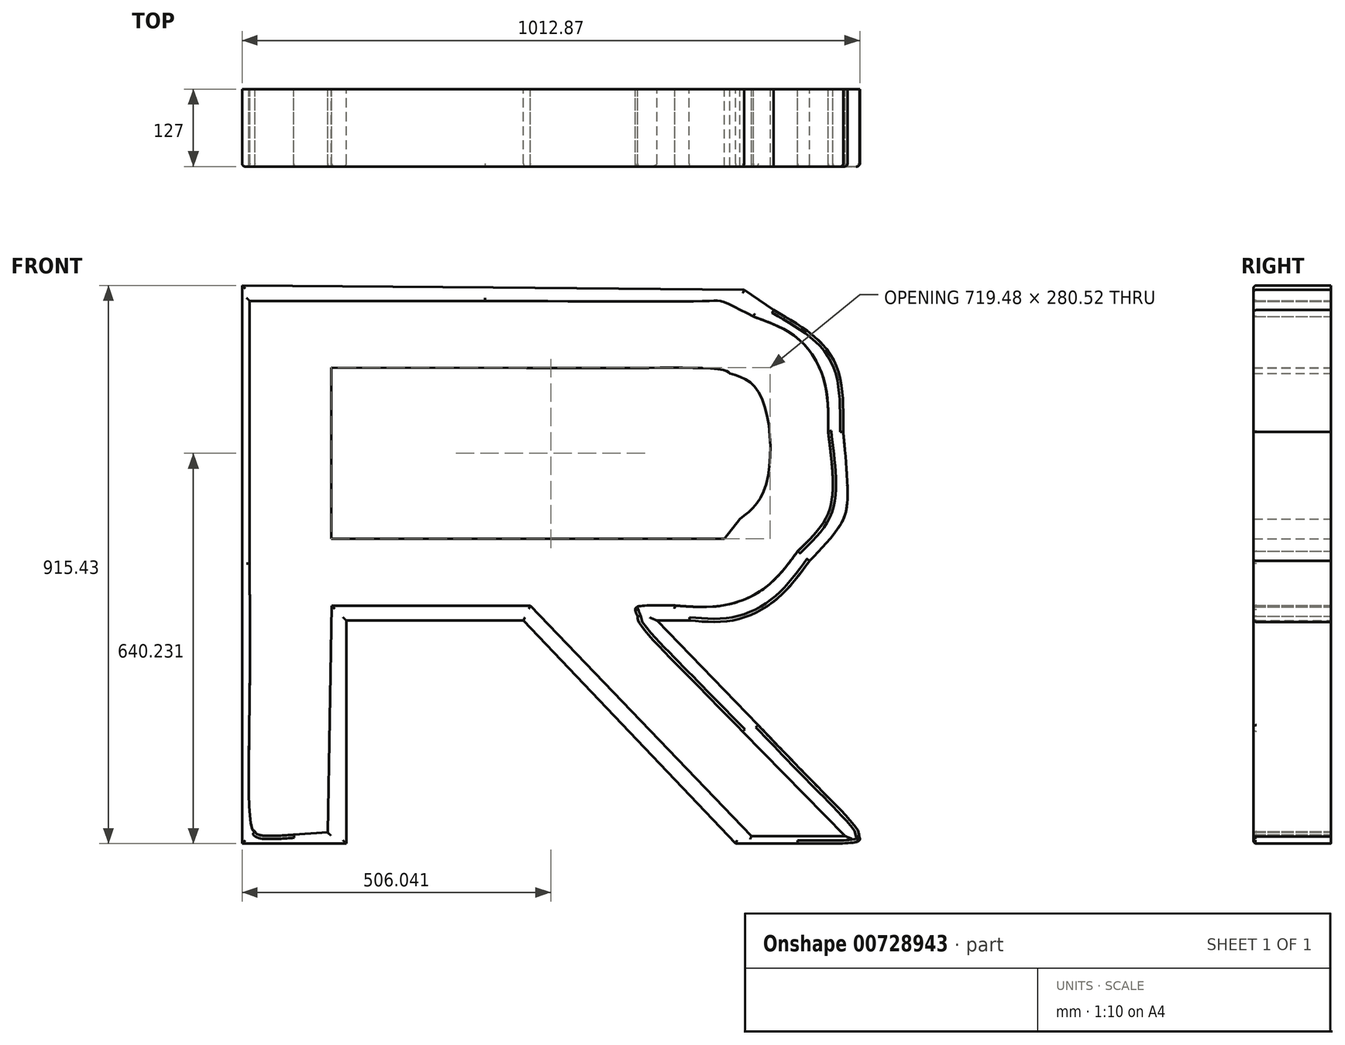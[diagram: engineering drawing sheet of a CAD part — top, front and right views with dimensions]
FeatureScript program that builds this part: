
annotation { "Feature Type Name" : "Feature", "Feature Type Description" : "" }
export const myFeature = defineFeature(function(context is Context, id is Id, definition is map)
    precondition{}
    {
        {
            var Q0;
            Q0=qCreatedBy(makeId("Front.planeOp"),FACE);
            var sketch = newSketch(context, id + "F0", { "sketchPlane" : qUnion([Q0])});
            skFitSpline(sketch, "E0", {"points": [v(-4513.08, -1878.1) * mm, v(-4548.72, -1872.9) * mm, v(-4580.06, -1866.5) * mm, v(-4582.7, -1863.84) * mm]});
            skFitSpline(sketch, "E1", {"points": [v(-4582.7, -1863.84) * mm, v(-4587.16, -1859.4) * mm, v(-4686.02, -165.4) * mm, v(-4686.02, -93.63) * mm]});
            skFitSpline(sketch, "E2", {"points": [v(-4686.02, -93.63) * mm, v(-4686.02, -76.02) * mm, v(-4679.1, -61.78) * mm, v(-4670.55, -61.78) * mm]});
            skFitSpline(sketch, "E3", {"points": [v(-4670.55, -61.78) * mm, v(-4662.04, -61.78) * mm, v(-4570.6, -244.2) * mm, v(-4467.36, -467.16) * mm]});
            skFitSpline(sketch, "E4", {"points": [v(-4467.36, -467.16) * mm, v(-4364.12, -690.12) * mm, v(-4179.05, -1088.06) * mm, v(-4056.11, -1351.47) * mm]});
            skFitSpline(sketch, "E5", {"points": [v(-4056.11, -1351.47) * mm, v(-3933.17, -1614.87) * mm, v(-3832.58, -1840.38) * mm, v(-3832.58, -1852.6) * mm]});
            skFitSpline(sketch, "E6", {"points": [v(-3832.58, -1852.6) * mm, v(-3832.58, -1871.46) * mm, v(-3846.64, -1876) * mm, v(-3925.86, -1882.7) * mm]});
            skFitSpline(sketch, "E7", {"points": [v(-3925.86, -1882.7) * mm, v(-4048.62, -1893.07) * mm, v(-4430.8, -1890.08) * mm, v(-4513.08, -1878.1) * mm]});
            skFitSpline(sketch, "E8", {"points": [v(-3879.02, -1844.36) * mm, v(-3866.96, -1832.3) * mm, v(-3906.6, -1744.18) * mm, v(-4421.11, -639.04) * mm]});
            skFitSpline(sketch, "E9", {"points": [v(-4421.11, -639.04) * mm, v(-4595.2, -265.1) * mm, v(-4644.19, -169.51) * mm, v(-4647.22, -197.77) * mm]});
            skFitSpline(sketch, "E10", {"points": [v(-4647.22, -197.77) * mm, v(-4650.89, -231.93) * mm, v(-4564.93, -1832.53) * mm, v(-4559.1, -1838.57) * mm]});
            skFitSpline(sketch, "E11", {"points": [v(-4559.1, -1838.57) * mm, v(-4534.28, -1864.33) * mm, v(-3904.35, -1869.69) * mm, v(-3879.02, -1844.36) * mm]});
            skFitSpline(sketch, "E12", {"points": [v(-5033.5, -1799.55) * mm, v(-5198.5, -1753.5) * mm, v(-5300.18, -1716.7) * mm, v(-5421.74, -1659.07) * mm]});
            skFitSpline(sketch, "E13", {"points": [v(-5421.74, -1659.07) * mm, v(-5492.65, -1625.45) * mm, v(-5504.3, -1615.6) * mm, v(-5499.25, -1593.5) * mm]});
            skFitSpline(sketch, "E14", {"points": [v(-5499.25, -1593.5) * mm, v(-5494.86, -1574.27) * mm, v(-5054.5, -397.2) * mm, v(-4942.58, -105.51) * mm]});
            skFitSpline(sketch, "E15", {"points": [v(-4942.58, -105.51) * mm, v(-4906.1, -10.43) * mm, v(-4900.2, -88.58) * mm, v(-4878.5, -955.17) * mm]});
            skFitSpline(sketch, "E16", {"points": [v(-4878.5, -955.17) * mm, v(-4866.7, -1426.06) * mm, v(-4859.55, -1818.19) * mm, v(-4862.6, -1826.57) * mm]});
            skFitSpline(sketch, "E17", {"points": [v(-4862.6, -1826.57) * mm, v(-4869.7, -1846.13) * mm, v(-4862.58, -1847.26) * mm, v(-5033.5, -1799.55) * mm]});
            skFitSpline(sketch, "E18", {"points": [v(-4886.44, -1747.32) * mm, v(-4889.85, -1715.47) * mm, v(-4898.96, -1379.43) * mm, v(-4906.7, -1000.56) * mm]});
            skFitSpline(sketch, "E19", {"points": [v(-4906.7, -1000.56) * mm, v(-4914.43, -621.7) * mm, v(-4924.18, -280.69) * mm, v(-4928.36, -242.77) * mm]});
            skFitSpline(sketch, "E20", {"points": [v(-5195.5, -864.56) * mm, v(-5338.25, -1244.47) * mm, v(-5458.03, -1566.94) * mm, v(-5461.69, -1581.16) * mm]});
            skFitSpline(sketch, "E21", {"points": [v(-5461.69, -1581.16) * mm, v(-5467.6, -1604.15) * mm, v(-5453.6, -1613.24) * mm, v(-5335.45, -1663.1) * mm]});
            skFitSpline(sketch, "E22", {"points": [v(-5335.45, -1663.1) * mm, v(-5217.3, -1712.99) * mm, v(-4937.34, -1803.14) * mm, v(-4895.91, -1804.66) * mm]});
            skFitSpline(sketch, "E23", {"points": [v(-4895.91, -1804.66) * mm, v(-4884.45, -1805.08) * mm, v(-4881.9, -1789.73) * mm, v(-4886.44, -1747.32) * mm]});
            skLineSegment(sketch, "E24", {"start": v(-4928.36, -242.77) * mm, "end": v(-4935.96, -173.83) * mm});
            skLineSegment(sketch, "E25", {"start": v(-4935.96, -173.83) * mm, "end": v(-5195.5, -864.56) * mm});
            skFitSpline(sketch, "E26", {"points": [v(-5758.92, -1450.29) * mm, v(-5985.16, -1262.43) * mm, v(-6141.2, -1100.12) * mm, v(-6134.22, -1059.86) * mm]});
            skFitSpline(sketch, "E27", {"points": [v(-6134.22, -1059.86) * mm, v(-6131.22, -1042.48) * mm, v(-5234.38, -58.31) * mm, v(-5181.72, -14.6) * mm]});
            skFitSpline(sketch, "E28", {"points": [v(-5181.72, -14.6) * mm, v(-5164.94, -0.68) * mm, v(-5160.85, -0.7) * mm, v(-5155.78, -14.68) * mm]});
            skFitSpline(sketch, "E29", {"points": [v(-5155.78, -14.68) * mm, v(-5146.02, -41.6) * mm, v(-5688.86, -1469.2) * mm, v(-5710.15, -1472.64) * mm]});
            skFitSpline(sketch, "E30", {"points": [v(-5710.15, -1472.64) * mm, v(-5720.2, -1474.27) * mm, v(-5742.15, -1464.2) * mm, v(-5758.92, -1450.29) * mm]});
            skFitSpline(sketch, "E31", {"points": [v(-5583.89, -1110.3) * mm, v(-5340.19, -464.36) * mm, v(-5189.83, -61.78) * mm, v(-5192.28, -61.78) * mm]});
            skFitSpline(sketch, "E32", {"points": [v(-5192.28, -61.78) * mm, v(-5193.68, -61.78) * mm, v(-5375.19, -257.92) * mm, v(-5595.63, -497.64) * mm]});
            skFitSpline(sketch, "E33", {"points": [v(-5595.63, -497.64) * mm, v(-5816.08, -737.37) * mm, v(-6023.27, -962.22) * mm, v(-6056.06, -997.33) * mm]});
            skFitSpline(sketch, "E34", {"points": [v(-6080.96, -1107.05) * mm, v(-5997.1, -1217.95) * mm, v(-5722.2, -1461.2) * mm, v(-5709.04, -1436.14) * mm]});
            skFitSpline(sketch, "E35", {"points": [v(-5709.04, -1436.14) * mm, v(-5704.72, -1427.92) * mm, v(-5648.4, -1281.28) * mm, v(-5583.89, -1110.3) * mm]});
            skLineSegment(sketch, "E36", {"start": v(-6056.06, -997.33) * mm, "end": v(-6115.67, -1061.15) * mm});
            skLineSegment(sketch, "E37", {"start": v(-6115.67, -1061.15) * mm, "end": v(-6080.96, -1107.05) * mm});
            skFitSpline(sketch, "E38", {"points": [v(-6376.64, -717.1) * mm, v(-6465.1, -554.38) * mm, v(-6517.72, -425.18) * mm, v(-6512.5, -383.52) * mm]});
            skFitSpline(sketch, "E39", {"points": [v(-6512.5, -383.52) * mm, v(-6509.12, -356.55) * mm, v(-6448.9, -325.3) * mm, v(-5938.45, -85.66) * mm]});
            skFitSpline(sketch, "E40", {"points": [v(-5938.45, -85.66) * mm, v(-5624.8, 61.59) * mm, v(-5362.42, 182.06) * mm, v(-5355.38, 182.06) * mm]});
            skFitSpline(sketch, "E41", {"points": [v(-5355.38, 182.06) * mm, v(-5348.35, 182.06) * mm, v(-5344.37, 174.42) * mm, v(-5346.54, 165.09) * mm]});
            skFitSpline(sketch, "E42", {"points": [v(-5346.54, 165.09) * mm, v(-5353.35, 135.75) * mm, v(-6262.79, -854.26) * mm, v(-6282.92, -854.26) * mm]});
            skFitSpline(sketch, "E43", {"points": [v(-6282.92, -854.26) * mm, v(-6294.77, -854.26) * mm, v(-6330.5, -801.99) * mm, v(-6376.64, -717.1) * mm]});
            skFitSpline(sketch, "E44", {"points": [v(-5831.8, -342.2) * mm, v(-5615.18, -104.15) * mm, v(-5427.1, 102.77) * mm, v(-5413.85, 117.6) * mm]});
            skFitSpline(sketch, "E45", {"points": [v(-5413.85, 117.6) * mm, v(-5398.94, 134.3) * mm, v(-5598.63, 46.37) * mm, v(-5937.04, -112.76) * mm]});
            skFitSpline(sketch, "E46", {"points": [v(-5937.04, -112.76) * mm, v(-6238.06, -254.3) * mm, v(-6486.6, -372.02) * mm, v(-6489.34, -374.36) * mm]});
            skFitSpline(sketch, "E47", {"points": [v(-6489.34, -374.36) * mm, v(-6506.31, -388.79) * mm, v(-6417.14, -598.64) * mm, v(-6332.34, -743.85) * mm]});
            skFitSpline(sketch, "E48", {"points": [v(-6253.05, -803.85) * mm, v(-6237.97, -787.99) * mm, v(-6048.41, -580.24) * mm, v(-5831.8, -342.2) * mm]});
            skLineSegment(sketch, "E49", {"start": v(-6332.34, -743.85) * mm, "end": v(-6280.45, -832.7) * mm});
            skLineSegment(sketch, "E50", {"start": v(-6280.45, -832.7) * mm, "end": v(-6253.05, -803.85) * mm});
            skFitSpline(sketch, "E51", {"points": [v(3214.4, -607.33) * mm, v(3181.1, -589.95) * mm, v(3147.6, -532.2) * mm, v(3159.56, -512.83) * mm]});
            skFitSpline(sketch, "E52", {"points": [v(3159.56, -512.83) * mm, v(3171.55, -493.43) * mm, v(3228.61, -498.8) * mm, v(3244.73, -520.84) * mm]});
            skFitSpline(sketch, "E53", {"points": [v(3244.73, -520.84) * mm, v(3253.05, -532.22) * mm, v(3265.83, -537.06) * mm, v(3274.1, -531.95) * mm]});
            skFitSpline(sketch, "E54", {"points": [v(3274.1, -531.95) * mm, v(3292.4, -520.64) * mm, v(3269.27, -488.5) * mm, v(3242.83, -488.5) * mm]});
            skFitSpline(sketch, "E55", {"points": [v(3242.83, -488.5) * mm, v(3212.18, -488.5) * mm, v(3165.63, -430.83) * mm, v(3165.63, -392.87) * mm]});
            skFitSpline(sketch, "E56", {"points": [v(3165.63, -392.87) * mm, v(3165.63, -335.43) * mm, v(3202.8, -300.08) * mm, v(3263.16, -300.08) * mm]});
            skFitSpline(sketch, "E57", {"points": [v(3263.16, -300.08) * mm, v(3302.3, -300.08) * mm, v(3320.03, -306.86) * mm, v(3337.62, -328.58) * mm]});
            skFitSpline(sketch, "E58", {"points": [v(3337.62, -328.58) * mm, v(3375.45, -375.3) * mm, v(3368.13, -403.15) * mm, v(3318.03, -403.15) * mm]});
            skFitSpline(sketch, "E59", {"points": [v(3318.03, -403.15) * mm, v(3294.56, -403.15) * mm, v(3275.36, -397.67) * mm, v(3275.36, -390.96) * mm]});
            skFitSpline(sketch, "E60", {"points": [v(3275.36, -390.96) * mm, v(3275.36, -384.26) * mm, v(3269.87, -378.77) * mm, v(3263.16, -378.77) * mm]});
            skFitSpline(sketch, "E61", {"points": [v(3263.16, -378.77) * mm, v(3234.41, -378.77) * mm, v(3254.73, -400.93) * mm, v(3299.66, -418.58) * mm]});
            skFitSpline(sketch, "E62", {"points": [v(3299.66, -418.58) * mm, v(3354.1, -439.97) * mm, v(3378.57, -483.66) * mm, v(3366.6, -538.12) * mm]});
            skFitSpline(sketch, "E63", {"points": [v(3366.6, -538.12) * mm, v(3352.4, -602.85) * mm, v(3274.05, -638.47) * mm, v(3214.4, -607.33) * mm]});
            skFitSpline(sketch, "E64", {"points": [v(3317.82, -566.22) * mm, v(3329.82, -554.21) * mm, v(3336.17, -531.45) * mm, v(3333.93, -508.46) * mm]});
            skFitSpline(sketch, "E65", {"points": [v(3333.93, -508.46) * mm, v(3330.95, -478) * mm, v(3319.87, -464.82) * mm, v(3277.73, -441.64) * mm]});
            skFitSpline(sketch, "E66", {"points": [v(3277.73, -441.64) * mm, v(3237.65, -419.6) * mm, v(3226.11, -406.58) * mm, v(3228.96, -386.63) * mm]});
            skFitSpline(sketch, "E67", {"points": [v(3228.96, -386.63) * mm, v(3233.27, -356.35) * mm, v(3285.18, -343.03) * mm, v(3300.75, -368.2) * mm]});
            skFitSpline(sketch, "E68", {"points": [v(3300.75, -368.2) * mm, v(3306.17, -376.98) * mm, v(3314.43, -380.34) * mm, v(3319.1, -375.66) * mm]});
            skFitSpline(sketch, "E69", {"points": [v(3319.1, -375.66) * mm, v(3323.78, -371) * mm, v(3320.43, -358.53) * mm, v(3311.66, -347.96) * mm]});
            skFitSpline(sketch, "E70", {"points": [v(3311.66, -347.96) * mm, v(3287.48, -318.83) * mm, v(3224.3, -329.53) * mm, v(3206.32, -365.8) * mm]});
            skFitSpline(sketch, "E71", {"points": [v(3206.32, -365.8) * mm, v(3186.57, -405.64) * mm, v(3202.8, -433.32) * mm, v(3264.32, -464.7) * mm]});
            skFitSpline(sketch, "E72", {"points": [v(3264.32, -464.7) * mm, v(3305.7, -485.82) * mm, v(3312.83, -494.93) * mm, v(3309.63, -522.66) * mm]});
            skFitSpline(sketch, "E73", {"points": [v(3309.63, -522.66) * mm, v(3306.49, -549.91) * mm, v(3299.03, -556.21) * mm, v(3266.13, -559.38) * mm]});
            skFitSpline(sketch, "E74", {"points": [v(3266.13, -559.38) * mm, v(3238.78, -562.02) * mm, v(3224.14, -557.27) * mm, v(3219.1, -544.14) * mm]});
            skFitSpline(sketch, "E75", {"points": [v(3219.1, -544.14) * mm, v(3211.2, -523.53) * mm, v(3190.01, -517.9) * mm, v(3190.01, -536.4) * mm]});
            skFitSpline(sketch, "E76", {"points": [v(3190.01, -536.4) * mm, v(3190.01, -580.85) * mm, v(3281.77, -602.26) * mm, v(3317.82, -566.22) * mm]});
            skFitSpline(sketch, "E77", {"points": [v(5507.24, -600.33) * mm, v(5430.62, -559.24) * mm, v(5401.78, -465.95) * mm, v(5440.49, -384.37) * mm]});
            skFitSpline(sketch, "E78", {"points": [v(5440.49, -384.37) * mm, v(5486.58, -287.24) * mm, v(5615.75, -267.6) * mm, v(5698.52, -345.13) * mm]});
            skFitSpline(sketch, "E79", {"points": [v(5698.52, -345.13) * mm, v(5740.21, -384.19) * mm, v(5734.76, -415.43) * mm, v(5686.32, -414.96) * mm]});
            skFitSpline(sketch, "E80", {"points": [v(5686.32, -414.96) * mm, v(5664.53, -414.75) * mm, v(5636.05, -406.52) * mm, v(5623.03, -396.67) * mm]});
            skFitSpline(sketch, "E81", {"points": [v(5623.03, -396.67) * mm, v(5610.02, -386.83) * mm, v(5589.44, -378.77) * mm, v(5577.31, -378.77) * mm]});
            skFitSpline(sketch, "E82", {"points": [v(5577.31, -378.77) * mm, v(5546.4, -378.77) * mm, v(5506.5, -422.12) * mm, v(5506.5, -455.72) * mm]});
            skFitSpline(sketch, "E83", {"points": [v(5506.5, -455.72) * mm, v(5506.5, -517.6) * mm, v(5592.51, -562.23) * mm, v(5628.41, -518.98) * mm]});
            skFitSpline(sketch, "E84", {"points": [v(5628.41, -518.98) * mm, v(5648.4, -494.89) * mm, v(5712.42, -495.2) * mm, v(5721.71, -519.43) * mm]});
            skFitSpline(sketch, "E85", {"points": [v(5721.71, -519.43) * mm, v(5736.2, -557.18) * mm, v(5644.3, -622.6) * mm, v(5576.8, -622.6) * mm]});
            skFitSpline(sketch, "E86", {"points": [v(5576.8, -622.6) * mm, v(5561.4, -622.6) * mm, v(5530.1, -612.58) * mm, v(5507.24, -600.33) * mm]});
            skFitSpline(sketch, "E87", {"points": [v(5646.13, -571.89) * mm, v(5663.2, -564.1) * mm, v(5677.18, -552.54) * mm, v(5677.18, -546.2) * mm]});
            skFitSpline(sketch, "E88", {"points": [v(5677.18, -546.2) * mm, v(5677.18, -539.76) * mm, v(5667.74, -538.8) * mm, v(5655.84, -544.03) * mm]});
            skFitSpline(sketch, "E89", {"points": [v(5655.84, -544.03) * mm, v(5560.75, -585.8) * mm, v(5482.1, -547.64) * mm, v(5482.1, -459.73) * mm]});
            skFitSpline(sketch, "E90", {"points": [v(5482.1, -459.73) * mm, v(5482.1, -394.34) * mm, v(5519.02, -354.39) * mm, v(5579.44, -354.39) * mm]});
            skFitSpline(sketch, "E91", {"points": [v(5579.44, -354.39) * mm, v(5603.81, -354.39) * mm, v(5634.4, -362.44) * mm, v(5647.42, -372.29) * mm]});
            skFitSpline(sketch, "E92", {"points": [v(5647.42, -372.29) * mm, v(5677.34, -394.92) * mm, v(5690.42, -395.69) * mm, v(5682.22, -374.33) * mm]});
            skFitSpline(sketch, "E93", {"points": [v(5682.22, -374.33) * mm, v(5673.25, -350.95) * mm, v(5622.4, -330) * mm, v(5574.62, -330) * mm]});
            skFitSpline(sketch, "E94", {"points": [v(5574.62, -330) * mm, v(5461.37, -330) * mm, v(5412.53, -481.37) * mm, v(5500.86, -558.6) * mm]});
            skFitSpline(sketch, "E95", {"points": [v(5500.86, -558.6) * mm, v(5535.7, -589.07) * mm, v(5596.26, -594.6) * mm, v(5646.13, -571.89) * mm]});
            skFitSpline(sketch, "E96", {"points": [v(6475.76, -608.53) * mm, v(6440.32, -589.15) * mm, v(6420.9, -560.93) * mm, v(6420.9, -528.84) * mm]});
            skFitSpline(sketch, "E97", {"points": [v(6420.9, -528.84) * mm, v(6420.9, -505.63) * mm, v(6427.37, -500.7) * mm, v(6457.85, -500.7) * mm]});
            skFitSpline(sketch, "E98", {"points": [v(6457.85, -500.7) * mm, v(6479.46, -500.7) * mm, v(6497.73, -508.29) * mm, v(6501.83, -518.98) * mm]});
            skFitSpline(sketch, "E99", {"points": [v(6501.83, -518.98) * mm, v(6510.56, -541.73) * mm, v(6542.81, -543.18) * mm, v(6542.81, -520.83) * mm]});
            skFitSpline(sketch, "E100", {"points": [v(6542.81, -520.83) * mm, v(6542.81, -511.79) * mm, v(6520.9, -495.78) * mm, v(6494.13, -485.27) * mm]});
            skFitSpline(sketch, "E101", {"points": [v(6494.13, -485.27) * mm, v(6414.12, -453.84) * mm, v(6400.9, -369.27) * mm, v(6467.8, -316.66) * mm]});
            skFitSpline(sketch, "E102", {"points": [v(6467.8, -316.66) * mm, v(6521.92, -274.08) * mm, v(6615.96, -310.83) * mm, v(6615.96, -374.56) * mm]});
            skFitSpline(sketch, "E103", {"points": [v(6615.96, -374.56) * mm, v(6615.96, -397.75) * mm, v(6609.51, -403.15) * mm, v(6581.83, -403.15) * mm]});
            skFitSpline(sketch, "E104", {"points": [v(6581.83, -403.15) * mm, v(6563.05, -403.15) * mm, v(6541.1, -396.57) * mm, v(6533.06, -388.52) * mm]});
            skFitSpline(sketch, "E105", {"points": [v(6533.06, -388.52) * mm, v(6523.5, -378.97) * mm, v(6518.43, -378.46) * mm, v(6518.43, -387.05) * mm]});
            skFitSpline(sketch, "E106", {"points": [v(6518.43, -387.05) * mm, v(6518.43, -394.28) * mm, v(6535.1, -407.1) * mm, v(6555.49, -415.55) * mm]});
            skFitSpline(sketch, "E107", {"points": [v(6555.49, -415.55) * mm, v(6634.58, -448.3) * mm, v(6651.74, -527.75) * mm, v(6592.52, -586.97) * mm]});
            skFitSpline(sketch, "E108", {"points": [v(6592.52, -586.97) * mm, v(6555.36, -624.13) * mm, v(6517.17, -631.19) * mm, v(6475.76, -608.53) * mm]});
            skFitSpline(sketch, "E109", {"points": [v(6589, -546.64) * mm, v(6610.12, -502.37) * mm, v(6593.07, -471.59) * mm, v(6529.45, -439.13) * mm]});
            skFitSpline(sketch, "E110", {"points": [v(6529.45, -439.13) * mm, v(6491.43, -419.74) * mm, v(6481.19, -408.01) * mm, v(6484.14, -387.28) * mm]});
            skFitSpline(sketch, "E111", {"points": [v(6484.14, -387.28) * mm, v(6488.42, -357.15) * mm, v(6540.07, -342.42) * mm, v(6555.26, -367) * mm]});
            skFitSpline(sketch, "E112", {"points": [v(6555.26, -367) * mm, v(6560.28, -375.1) * mm, v(6571.23, -379.46) * mm, v(6579.61, -376.66) * mm]});
            skFitSpline(sketch, "E113", {"points": [v(6579.61, -376.66) * mm, v(6605.96, -367.88) * mm, v(6556.8, -330) * mm, v(6519.05, -330) * mm]});
            skFitSpline(sketch, "E114", {"points": [v(6519.05, -330) * mm, v(6476.1, -330) * mm, v(6454.56, -355.13) * mm, v(6459.64, -399.34) * mm]});
            skFitSpline(sketch, "E115", {"points": [v(6459.64, -399.34) * mm, v(6462.6, -425.11) * mm, v(6475.62, -439.81) * mm, v(6512.33, -458.8) * mm]});
            skFitSpline(sketch, "E116", {"points": [v(6512.33, -458.8) * mm, v(6552.4, -479.54) * mm, v(6561.1, -490.41) * mm, v(6561.1, -519.8) * mm]});
            skFitSpline(sketch, "E117", {"points": [v(6561.1, -519.8) * mm, v(6561.1, -547.97) * mm, v(6555.07, -556.4) * mm, v(6532.66, -559.58) * mm]});
            skFitSpline(sketch, "E118", {"points": [v(6532.66, -559.58) * mm, v(6517.02, -561.8) * mm, v(6493.67, -554.06) * mm, v(6480.77, -542.38) * mm]});
            skFitSpline(sketch, "E119", {"points": [v(6480.77, -542.38) * mm, v(6449.35, -513.95) * mm, v(6435.36, -530.48) * mm, v(6464.03, -562.17) * mm]});
            skFitSpline(sketch, "E120", {"points": [v(6464.03, -562.17) * mm, v(6497.9, -599.59) * mm, v(6567.9, -590.9) * mm, v(6589, -546.64) * mm]});
            skFitSpline(sketch, "E121", {"points": [v(2275.61, -458.02) * mm, v(2275.61, -380.8) * mm, v(2270.77, -330) * mm, v(2263.42, -330) * mm]});
            skFitSpline(sketch, "E122", {"points": [v(2263.42, -330) * mm, v(2256.07, -330) * mm, v(2251.23, -380.8) * mm, v(2251.23, -458.02) * mm]});
            skFitSpline(sketch, "E123", {"points": [v(2251.23, -458.02) * mm, v(2251.23, -535.23) * mm, v(2256.07, -586.03) * mm, v(2263.42, -586.03) * mm]});
            skFitSpline(sketch, "E124", {"points": [v(2263.42, -586.03) * mm, v(2270.77, -586.03) * mm, v(2275.61, -535.23) * mm, v(2275.61, -458.02) * mm]});
            skLineSegment(sketch, "E125", {"start": v(2226.84, -458.02) * mm, "end": v(2226.84, -305.62) * mm});
            skLineSegment(sketch, "E126", {"start": v(2226.84, -305.62) * mm, "end": v(2263.42, -305.62) * mm});
            skLineSegment(sketch, "E127", {"start": v(2263.42, -305.62) * mm, "end": v(2300, -305.62) * mm});
            skLineSegment(sketch, "E128", {"start": v(2300, -305.62) * mm, "end": v(2300, -458.02) * mm});
            skLineSegment(sketch, "E129", {"start": v(2300, -458.02) * mm, "end": v(2300, -610.42) * mm});
            skLineSegment(sketch, "E130", {"start": v(2300, -610.42) * mm, "end": v(2263.42, -610.42) * mm});
            skLineSegment(sketch, "E131", {"start": v(2263.42, -610.42) * mm, "end": v(2226.84, -610.42) * mm});
            skLineSegment(sketch, "E132", {"start": v(2226.84, -610.42) * mm, "end": v(2226.84, -458.02) * mm});
            skFitSpline(sketch, "E133", {"points": [v(2616.99, -500.39) * mm, v(2616.99, -393.45) * mm, v(2616.11, -390.02) * mm, v(2585.66, -378.45) * mm]});
            skFitSpline(sketch, "E134", {"points": [v(2585.66, -378.45) * mm, v(2562.68, -369.7) * mm, v(2555.37, -359.24) * mm, v(2558.23, -339.13) * mm]});
            skFitSpline(sketch, "E135", {"points": [v(2558.23, -339.13) * mm, v(2561.87, -313.49) * mm, v(2568.04, -311.71) * mm, v(2653.56, -311.71) * mm]});
            skFitSpline(sketch, "E136", {"points": [v(2653.56, -311.71) * mm, v(2739.09, -311.71) * mm, v(2745.26, -313.49) * mm, v(2748.9, -339.13) * mm]});
            skFitSpline(sketch, "E137", {"points": [v(2748.9, -339.13) * mm, v(2751.76, -359.24) * mm, v(2744.45, -369.7) * mm, v(2721.47, -378.45) * mm]});
            skFitSpline(sketch, "E138", {"points": [v(2721.47, -378.45) * mm, v(2691.02, -390.02) * mm, v(2690.14, -393.45) * mm, v(2690.14, -500.39) * mm]});
            skFitSpline(sketch, "E139", {"points": [v(2665.76, -475.16) * mm, v(2665.76, -374.55) * mm, v(2668.01, -363.7) * mm, v(2690.14, -357.92) * mm]});
            skFitSpline(sketch, "E140", {"points": [v(2690.14, -357.92) * mm, v(2735.72, -346) * mm, v(2714.75, -330) * mm, v(2653.56, -330) * mm]});
            skFitSpline(sketch, "E141", {"points": [v(2653.56, -330) * mm, v(2592.37, -330) * mm, v(2571.41, -346) * mm, v(2616.99, -357.92) * mm]});
            skFitSpline(sketch, "E142", {"points": [v(2616.99, -357.92) * mm, v(2639.12, -363.7) * mm, v(2641.37, -374.55) * mm, v(2641.37, -475.16) * mm]});
            skFitSpline(sketch, "E143", {"points": [v(2641.37, -475.16) * mm, v(2641.37, -540.95) * mm, v(2646.33, -586.03) * mm, v(2653.56, -586.03) * mm]});
            skFitSpline(sketch, "E144", {"points": [v(2653.56, -586.03) * mm, v(2660.8, -586.03) * mm, v(2665.76, -540.95) * mm, v(2665.76, -475.16) * mm]});
            skLineSegment(sketch, "E145", {"start": v(2690.14, -500.39) * mm, "end": v(2690.14, -610.42) * mm});
            skLineSegment(sketch, "E146", {"start": v(2690.14, -610.42) * mm, "end": v(2653.56, -610.42) * mm});
            skLineSegment(sketch, "E147", {"start": v(2653.56, -610.42) * mm, "end": v(2616.99, -610.42) * mm});
            skLineSegment(sketch, "E148", {"start": v(2616.99, -610.42) * mm, "end": v(2616.99, -500.39) * mm});
            skFitSpline(sketch, "E149", {"points": [v(3717.32, -308.13) * mm, v(3802.52, -311.58) * mm, v(3805.7, -312.81) * mm, v(3805.7, -342.2) * mm]});
            skFitSpline(sketch, "E150", {"points": [v(3805.7, -342.2) * mm, v(3805.7, -368.61) * mm, v(3799.62, -373.18) * mm, v(3759.99, -376.46) * mm]});
            skFitSpline(sketch, "E151", {"points": [v(3759.99, -376.46) * mm, v(3702.05, -381.25) * mm, v(3697.47, -412.18) * mm, v(3753.9, -417.62) * mm]});
            skFitSpline(sketch, "E152", {"points": [v(3753.9, -417.62) * mm, v(3788.73, -420.98) * mm, v(3793.98, -426.22) * mm, v(3797.34, -461.07) * mm]});
            skFitSpline(sketch, "E153", {"points": [v(3797.34, -461.07) * mm, v(3801, -499.07) * mm, v(3799.38, -500.7) * mm, v(3757.71, -500.7) * mm]});
            skFitSpline(sketch, "E154", {"points": [v(3757.71, -500.7) * mm, v(3696.23, -500.7) * mm, v(3698.2, -534.47) * mm, v(3759.99, -539.58) * mm]});
            skFitSpline(sketch, "E155", {"points": [v(3759.99, -539.58) * mm, v(3799.62, -542.86) * mm, v(3805.7, -547.42) * mm, v(3805.7, -573.84) * mm]});
            skFitSpline(sketch, "E156", {"points": [v(3805.7, -573.84) * mm, v(3805.7, -603.22) * mm, v(3802.52, -604.45) * mm, v(3717.32, -607.9) * mm]});
            skLineSegment(sketch, "E157", {"start": v(3628.92, -458.02) * mm, "end": v(3628.92, -304.55) * mm});
            skLineSegment(sketch, "E158", {"start": v(3628.92, -304.55) * mm, "end": v(3717.32, -308.13) * mm});
            skFitSpline(sketch, "E159", {"points": [v(3775.23, -574.58) * mm, v(3775.23, -568.28) * mm, v(3754.65, -561.42) * mm, v(3729.5, -559.34) * mm]});
            skFitSpline(sketch, "E160", {"points": [v(3729.5, -559.34) * mm, v(3687.68, -555.88) * mm, v(3683.79, -552.44) * mm, v(3683.79, -518.98) * mm]});
            skFitSpline(sketch, "E161", {"points": [v(3683.79, -518.98) * mm, v(3683.79, -485.51) * mm, v(3687.68, -482.08) * mm, v(3729.5, -478.62) * mm]});
            skFitSpline(sketch, "E162", {"points": [v(3729.5, -478.62) * mm, v(3754.65, -476.54) * mm, v(3775.23, -470.01) * mm, v(3775.23, -464.11) * mm]});
            skFitSpline(sketch, "E163", {"points": [v(3775.23, -464.11) * mm, v(3775.23, -458.22) * mm, v(3754.65, -451.7) * mm, v(3729.5, -449.61) * mm]});
            skFitSpline(sketch, "E164", {"points": [v(3729.5, -449.61) * mm, v(3686.1, -446.02) * mm, v(3683.79, -443.66) * mm, v(3683.79, -403.15) * mm]});
            skFitSpline(sketch, "E165", {"points": [v(3683.79, -403.15) * mm, v(3683.79, -362.64) * mm, v(3686.1, -360.3) * mm, v(3729.5, -356.7) * mm]});
            skFitSpline(sketch, "E166", {"points": [v(3729.5, -356.7) * mm, v(3797.09, -351.1) * mm, v(3785.04, -330) * mm, v(3714.27, -330) * mm]});
            skLineSegment(sketch, "E167", {"start": v(3717.32, -607.9) * mm, "end": v(3628.92, -611.49) * mm});
            skLineSegment(sketch, "E168", {"start": v(3628.92, -611.49) * mm, "end": v(3628.92, -458.02) * mm});
            skFitSpline(sketch, "E169", {"points": [v(3714.27, -586.03) * mm, v(3747.8, -586.03) * mm, v(3775.23, -580.88) * mm, v(3775.23, -574.58) * mm]});
            skLineSegment(sketch, "E170", {"start": v(3714.27, -330) * mm, "end": v(3653.3, -330) * mm});
            skLineSegment(sketch, "E171", {"start": v(3653.3, -330) * mm, "end": v(3653.3, -458.02) * mm});
            skLineSegment(sketch, "E172", {"start": v(3653.3, -458.02) * mm, "end": v(3653.3, -586.03) * mm});
            skLineSegment(sketch, "E173", {"start": v(3653.3, -586.03) * mm, "end": v(3714.27, -586.03) * mm});
            skFitSpline(sketch, "E174", {"points": [v(4159.83, -305.62) * mm, v(4228.3, -305.62) * mm, v(4243.88, -309.87) * mm, v(4269.56, -335.54) * mm]});
            skFitSpline(sketch, "E175", {"points": [v(4269.56, -335.54) * mm, v(4312.78, -378.77) * mm, v(4304.85, -462.75) * mm, v(4254.75, -492.31) * mm]});
            skFitSpline(sketch, "E176", {"points": [v(4254.75, -492.31) * mm, v(4241.02, -500.41) * mm, v(4242.45, -508.54) * mm, v(4262.62, -536.87) * mm]});
            skFitSpline(sketch, "E177", {"points": [v(4262.62, -536.87) * mm, v(4299.62, -588.82) * mm, v(4294.94, -610.42) * mm, v(4246.68, -610.42) * mm]});
            skFitSpline(sketch, "E178", {"points": [v(4246.68, -610.42) * mm, v(4215.33, -610.42) * mm, v(4202.17, -603.12) * mm, v(4188.95, -578.44) * mm]});
            skLineSegment(sketch, "E179", {"start": v(4080.03, -458.8) * mm, "end": v(4080.03, -305.62) * mm});
            skLineSegment(sketch, "E180", {"start": v(4080.03, -305.62) * mm, "end": v(4159.83, -305.62) * mm});
            skFitSpline(sketch, "E181", {"points": [v(4165.08, -575.39) * mm, v(4159.97, -597.25) * mm, v(4148.75, -605.26) * mm, v(4119.17, -608.14) * mm]});
            skLineSegment(sketch, "E182", {"start": v(4188.95, -578.44) * mm, "end": v(4171.84, -546.46) * mm});
            skLineSegment(sketch, "E183", {"start": v(4171.84, -546.46) * mm, "end": v(4165.08, -575.39) * mm});
            skFitSpline(sketch, "E184", {"points": [v(4128.8, -537.27) * mm, v(4128.8, -502.25) * mm, v(4133.9, -488.5) * mm, v(4146.91, -488.5) * mm]});
            skFitSpline(sketch, "E185", {"points": [v(4146.91, -488.5) * mm, v(4156.87, -488.5) * mm, v(4179.55, -510.44) * mm, v(4197.3, -537.27) * mm]});
            skFitSpline(sketch, "E186", {"points": [v(4197.3, -537.27) * mm, v(4215.05, -564.09) * mm, v(4234.33, -586.03) * mm, v(4240.14, -586.03) * mm]});
            skFitSpline(sketch, "E187", {"points": [v(4240.14, -586.03) * mm, v(4256.42, -586.03) * mm, v(4253.06, -576.03) * mm, v(4223.3, -535.78) * mm]});
            skLineSegment(sketch, "E188", {"start": v(4119.17, -608.14) * mm, "end": v(4080.03, -611.96) * mm});
            skLineSegment(sketch, "E189", {"start": v(4080.03, -611.96) * mm, "end": v(4080.03, -458.8) * mm});
            skFitSpline(sketch, "E190", {"points": [v(4229.4, -474.3) * mm, v(4254.46, -456.04) * mm, v(4262.9, -439.56) * mm, v(4262.9, -408.92) * mm]});
            skFitSpline(sketch, "E191", {"points": [v(4262.9, -408.92) * mm, v(4262.9, -356.66) * mm, v(4226.98, -330) * mm, v(4156.56, -330) * mm]});
            skLineSegment(sketch, "E192", {"start": v(4223.3, -535.78) * mm, "end": v(4195.9, -498.7) * mm});
            skLineSegment(sketch, "E193", {"start": v(4195.9, -498.7) * mm, "end": v(4229.4, -474.3) * mm});
            skFitSpline(sketch, "E194", {"points": [v(4104.41, -458.02) * mm, v(4104.41, -535.23) * mm, v(4109.25, -586.03) * mm, v(4116.6, -586.03) * mm]});
            skFitSpline(sketch, "E195", {"points": [v(4116.6, -586.03) * mm, v(4123.31, -586.03) * mm, v(4128.8, -564.09) * mm, v(4128.8, -537.27) * mm]});
            skLineSegment(sketch, "E196", {"start": v(4156.56, -330) * mm, "end": v(4104.41, -330) * mm});
            skLineSegment(sketch, "E197", {"start": v(4104.41, -330) * mm, "end": v(4104.41, -458.02) * mm});
            skFitSpline(sketch, "E198", {"points": [v(4133.6, -446.86) * mm, v(4129.96, -437.36) * mm, v(4128.76, -414.05) * mm, v(4130.93, -395.04) * mm]});
            skFitSpline(sketch, "E199", {"points": [v(4130.93, -395.04) * mm, v(4134.1, -367.4) * mm, v(4141.75, -359.7) * mm, v(4169.16, -356.55) * mm]});
            skFitSpline(sketch, "E200", {"points": [v(4169.16, -356.55) * mm, v(4188, -354.4) * mm, v(4211.32, -359.18) * mm, v(4220.97, -367.19) * mm]});
            skFitSpline(sketch, "E201", {"points": [v(4220.97, -367.19) * mm, v(4242.3, -384.9) * mm, v(4243.9, -429.49) * mm, v(4223.9, -449.48) * mm]});
            skFitSpline(sketch, "E202", {"points": [v(4223.9, -449.48) * mm, v(4203.69, -469.7) * mm, v(4141.67, -467.89) * mm, v(4133.6, -446.86) * mm]});
            skFitSpline(sketch, "E203", {"points": [v(4201.16, -428.28) * mm, v(4215.67, -419.1) * mm, v(4215.94, -413.91) * mm, v(4202.72, -397.99) * mm]});
            skFitSpline(sketch, "E204", {"points": [v(4202.72, -397.99) * mm, v(4179.58, -370.1) * mm, v(4165.37, -374.38) * mm, v(4165.37, -409.25) * mm]});
            skFitSpline(sketch, "E205", {"points": [v(4165.37, -409.25) * mm, v(4165.37, -441.79) * mm, v(4173.22, -445.96) * mm, v(4201.17, -428.28) * mm]});
            skFitSpline(sketch, "E206", {"points": [v(4587.56, -468.28) * mm, v(4557.04, -390.11) * mm, v(4534.93, -321.53) * mm, v(4538.42, -315.88) * mm]});
            skFitSpline(sketch, "E207", {"points": [v(4538.42, -315.88) * mm, v(4541.9, -310.24) * mm, v(4560.5, -305.62) * mm, v(4579.74, -305.62) * mm]});
            skFitSpline(sketch, "E208", {"points": [v(4579.74, -305.62) * mm, v(4611, -305.62) * mm, v(4617.41, -312.8) * mm, v(4639.99, -373.13) * mm]});
            skFitSpline(sketch, "E209", {"points": [v(4639.99, -373.13) * mm, v(4653.88, -410.26) * mm, v(4665.24, -445.93) * mm, v(4665.24, -452.38) * mm]});
            skFitSpline(sketch, "E210", {"points": [v(4665.24, -452.38) * mm, v(4665.24, -458.83) * mm, v(4670.73, -464.11) * mm, v(4677.44, -464.11) * mm]});
            skFitSpline(sketch, "E211", {"points": [v(4677.44, -464.11) * mm, v(4684.14, -464.11) * mm, v(4689.63, -458.83) * mm, v(4689.63, -452.38) * mm]});
            skFitSpline(sketch, "E212", {"points": [v(4689.63, -452.38) * mm, v(4689.63, -445.93) * mm, v(4701, -410.26) * mm, v(4714.89, -373.13) * mm]});
            skFitSpline(sketch, "E213", {"points": [v(4714.89, -373.13) * mm, v(4737.46, -312.8) * mm, v(4743.87, -305.62) * mm, v(4775.13, -305.62) * mm]});
            skFitSpline(sketch, "E214", {"points": [v(4775.13, -305.62) * mm, v(4794.37, -305.62) * mm, v(4812.96, -310.24) * mm, v(4816.45, -315.88) * mm]});
            skFitSpline(sketch, "E215", {"points": [v(4816.45, -315.88) * mm, v(4819.94, -321.53) * mm, v(4797.83, -390.11) * mm, v(4767.32, -468.28) * mm]});
            skFitSpline(sketch, "E216", {"points": [v(4767.32, -468.28) * mm, v(4714.74, -602.97) * mm, v(4710.03, -610.42) * mm, v(4677.44, -610.42) * mm]});
            skFitSpline(sketch, "E217", {"points": [v(4677.44, -610.42) * mm, v(4644.84, -610.42) * mm, v(4640.13, -602.97) * mm, v(4587.56, -468.28) * mm]});
            skFitSpline(sketch, "E218", {"points": [v(4736.89, -462) * mm, v(4764.46, -393.8) * mm, v(4784.67, -335.64) * mm, v(4781.8, -332.77) * mm]});
            skFitSpline(sketch, "E219", {"points": [v(4781.8, -332.77) * mm, v(4768.66, -319.63) * mm, v(4753.17, -347.64) * mm, v(4726.44, -432.88) * mm]});
            skFitSpline(sketch, "E220", {"points": [v(4726.44, -432.88) * mm, v(4705.8, -498.68) * mm, v(4691.78, -525.07) * mm, v(4677.44, -525.07) * mm]});
            skFitSpline(sketch, "E221", {"points": [v(4677.44, -525.07) * mm, v(4663.1, -525.07) * mm, v(4649.07, -498.68) * mm, v(4628.43, -432.88) * mm]});
            skFitSpline(sketch, "E222", {"points": [v(4628.43, -432.88) * mm, v(4601.7, -347.64) * mm, v(4586.2, -319.63) * mm, v(4573.07, -332.77) * mm]});
            skFitSpline(sketch, "E223", {"points": [v(4573.07, -332.77) * mm, v(4565.35, -340.49) * mm, v(4666.54, -586.03) * mm, v(4677.44, -586.03) * mm]});
            skFitSpline(sketch, "E224", {"points": [v(4677.44, -586.03) * mm, v(4682.56, -586.03) * mm, v(4709.31, -530.22) * mm, v(4736.89, -462) * mm]});
            skFitSpline(sketch, "E225", {"points": [v(5128.54, -458.02) * mm, v(5128.54, -380.8) * mm, v(5123.7, -330) * mm, v(5116.35, -330) * mm]});
            skFitSpline(sketch, "E226", {"points": [v(5116.35, -330) * mm, v(5109, -330) * mm, v(5104.16, -380.8) * mm, v(5104.16, -458.02) * mm]});
            skFitSpline(sketch, "E227", {"points": [v(5104.16, -458.02) * mm, v(5104.16, -535.23) * mm, v(5109, -586.03) * mm, v(5116.35, -586.03) * mm]});
            skFitSpline(sketch, "E228", {"points": [v(5116.35, -586.03) * mm, v(5123.7, -586.03) * mm, v(5128.54, -535.23) * mm, v(5128.54, -458.02) * mm]});
            skLineSegment(sketch, "E229", {"start": v(5079.77, -458.02) * mm, "end": v(5079.77, -305.62) * mm});
            skLineSegment(sketch, "E230", {"start": v(5079.77, -305.62) * mm, "end": v(5116.35, -305.62) * mm});
            skLineSegment(sketch, "E231", {"start": v(5116.35, -305.62) * mm, "end": v(5152.92, -305.62) * mm});
            skLineSegment(sketch, "E232", {"start": v(5152.92, -305.62) * mm, "end": v(5152.92, -458.02) * mm});
            skLineSegment(sketch, "E233", {"start": v(5152.92, -458.02) * mm, "end": v(5152.92, -610.42) * mm});
            skLineSegment(sketch, "E234", {"start": v(5152.92, -610.42) * mm, "end": v(5116.35, -610.42) * mm});
            skLineSegment(sketch, "E235", {"start": v(5116.35, -610.42) * mm, "end": v(5079.77, -610.42) * mm});
            skLineSegment(sketch, "E236", {"start": v(5079.77, -610.42) * mm, "end": v(5079.77, -458.02) * mm});
            skFitSpline(sketch, "E237", {"points": [v(6164.86, -342.2) * mm, v(6164.86, -376.74) * mm, v(6162.15, -378.77) * mm, v(6116.1, -378.77) * mm]});
            skFitSpline(sketch, "E238", {"points": [v(6116.1, -378.77) * mm, v(6054.5, -378.77) * mm, v(6046.72, -411.81) * mm, v(6106.95, -417.62) * mm]});
            skFitSpline(sketch, "E239", {"points": [v(6106.95, -417.62) * mm, v(6141.79, -420.98) * mm, v(6147.03, -426.22) * mm, v(6150.4, -461.07) * mm]});
            skFitSpline(sketch, "E240", {"points": [v(6150.4, -461.07) * mm, v(6154.06, -499.07) * mm, v(6152.44, -500.7) * mm, v(6110.77, -500.7) * mm]});
            skFitSpline(sketch, "E241", {"points": [v(6110.77, -500.7) * mm, v(6080.28, -500.7) * mm, v(6067.32, -506.14) * mm, v(6067.32, -518.98) * mm]});
            skFitSpline(sketch, "E242", {"points": [v(6067.32, -518.98) * mm, v(6067.32, -532.19) * mm, v(6080.87, -537.27) * mm, v(6116.1, -537.27) * mm]});
            skFitSpline(sketch, "E243", {"points": [v(6116.1, -537.27) * mm, v(6162.15, -537.27) * mm, v(6164.86, -539.3) * mm, v(6164.86, -573.84) * mm]});
            skLineSegment(sketch, "E244", {"start": v(5981.98, -458.02) * mm, "end": v(5981.98, -305.62) * mm});
            skLineSegment(sketch, "E245", {"start": v(5981.98, -305.62) * mm, "end": v(6073.42, -305.62) * mm});
            skLineSegment(sketch, "E246", {"start": v(6073.42, -305.62) * mm, "end": v(6164.86, -305.62) * mm});
            skLineSegment(sketch, "E247", {"start": v(6164.86, -305.62) * mm, "end": v(6164.86, -342.2) * mm});
            skFitSpline(sketch, "E248", {"points": [v(6140.48, -573.84) * mm, v(6140.48, -567.14) * mm, v(6118.53, -561.65) * mm, v(6091.7, -561.65) * mm]});
            skFitSpline(sketch, "E249", {"points": [v(6091.7, -561.65) * mm, v(6044.1, -561.65) * mm, v(6042.94, -560.63) * mm, v(6042.94, -518.98) * mm]});
            skFitSpline(sketch, "E250", {"points": [v(6042.94, -518.98) * mm, v(6042.94, -478.34) * mm, v(6044.97, -476.3) * mm, v(6085.61, -476.3) * mm]});
            skFitSpline(sketch, "E251", {"points": [v(6085.61, -476.3) * mm, v(6139.4, -476.3) * mm, v(6141.86, -454.78) * mm, v(6088.66, -449.65) * mm]});
            skFitSpline(sketch, "E252", {"points": [v(6088.66, -449.65) * mm, v(6052.49, -446.16) * mm, v(6048.7, -441.85) * mm, v(6045.25, -400.1) * mm]});
            skLineSegment(sketch, "E253", {"start": v(6164.86, -573.84) * mm, "end": v(6164.86, -610.42) * mm});
            skLineSegment(sketch, "E254", {"start": v(6164.86, -610.42) * mm, "end": v(6073.42, -610.42) * mm});
            skLineSegment(sketch, "E255", {"start": v(6073.42, -610.42) * mm, "end": v(5981.98, -610.42) * mm});
            skLineSegment(sketch, "E256", {"start": v(5981.98, -610.42) * mm, "end": v(5981.98, -458.02) * mm});
            skFitSpline(sketch, "E257", {"points": [v(6090.97, -354.39) * mm, v(6118.2, -354.39) * mm, v(6140.48, -348.9) * mm, v(6140.48, -342.2) * mm]});
            skFitSpline(sketch, "E258", {"points": [v(6140.48, -342.2) * mm, v(6140.48, -335.49) * mm, v(6110.3, -330) * mm, v(6073.42, -330) * mm]});
            skLineSegment(sketch, "E259", {"start": v(6045.25, -400.1) * mm, "end": v(6041.47, -354.39) * mm});
            skLineSegment(sketch, "E260", {"start": v(6041.47, -354.39) * mm, "end": v(6090.97, -354.39) * mm});
            skFitSpline(sketch, "E261", {"points": [v(6073.42, -586.03) * mm, v(6110.3, -586.03) * mm, v(6140.48, -580.55) * mm, v(6140.48, -573.84) * mm]});
            skLineSegment(sketch, "E262", {"start": v(6073.42, -330) * mm, "end": v(6006.36, -330) * mm});
            skLineSegment(sketch, "E263", {"start": v(6006.36, -330) * mm, "end": v(6006.36, -458.02) * mm});
            skLineSegment(sketch, "E264", {"start": v(6006.36, -458.02) * mm, "end": v(6006.36, -586.03) * mm});
            skLineSegment(sketch, "E265", {"start": v(6006.36, -586.03) * mm, "end": v(6073.42, -586.03) * mm});
            skFitSpline(sketch, "E266", {"points": [v(-4824.94, -178.62) * mm, v(-4852.57, 29.64) * mm, v(-4850.36, 23.57) * mm, v(-4898.42, 23.57) * mm]});
            skFitSpline(sketch, "E267", {"points": [v(-4898.42, 23.57) * mm, v(-4937.2, 23.57) * mm, v(-4941.14, 18.66) * mm, v(-5020.23, -128.18) * mm]});
            skFitSpline(sketch, "E268", {"points": [v(-5020.23, -128.18) * mm, v(-5080.64, -240.35) * mm, v(-5106.73, -278.1) * mm, v(-5120.24, -272.91) * mm]});
            skFitSpline(sketch, "E269", {"points": [v(-5120.24, -272.91) * mm, v(-5130.44, -269) * mm, v(-5135.43, -257.82) * mm, v(-5131.52, -247.64) * mm]});
            skFitSpline(sketch, "E270", {"points": [v(-5131.52, -247.64) * mm, v(-5119.23, -215.62) * mm, v(-5050.53, 63) * mm, v(-5054.28, 65.6) * mm]});
            skFitSpline(sketch, "E271", {"points": [v(-5054.28, 65.6) * mm, v(-5056.26, 66.97) * mm, v(-5078.44, 80.46) * mm, v(-5103.56, 95.57) * mm]});
            skFitSpline(sketch, "E272", {"points": [v(-5267.7, 24.54) * mm, v(-5332.85, -29.64) * mm, v(-5390.47, -73.97) * mm, v(-5395.75, -73.97) * mm]});
            skFitSpline(sketch, "E273", {"points": [v(-5395.75, -73.97) * mm, v(-5422.13, -73.97) * mm, v(-5396.87, -26.5) * mm, v(-5314.17, 79.3) * mm]});
            skLineSegment(sketch, "E274", {"start": v(-5103.56, 95.57) * mm, "end": v(-5149.25, 123.05) * mm});
            skLineSegment(sketch, "E275", {"start": v(-5149.25, 123.05) * mm, "end": v(-5267.7, 24.54) * mm});
            skFitSpline(sketch, "E276", {"points": [v(-5249.65, 232) * mm, v(-5264.31, 251.84) * mm, v(-5282.03, 265.94) * mm, v(-5289.01, 263.33) * mm]});
            skFitSpline(sketch, "E277", {"points": [v(-5289.01, 263.33) * mm, v(-5296, 260.73) * mm, v(-5366.1, 237.46) * mm, v(-5444.81, 211.63) * mm]});
            skFitSpline(sketch, "E278", {"points": [v(-5444.81, 211.63) * mm, v(-5648.2, 144.88) * mm, v(-5655.48, 165.48) * mm, v(-5468.09, 277.53) * mm]});
            skLineSegment(sketch, "E279", {"start": v(-5314.17, 79.3) * mm, "end": v(-5222.98, 195.94) * mm});
            skLineSegment(sketch, "E280", {"start": v(-5222.98, 195.94) * mm, "end": v(-5249.65, 232) * mm});
            skFitSpline(sketch, "E281", {"points": [v(-5501.84, 488.54) * mm, v(-5583.61, 499.53) * mm, v(-5653.88, 511.87) * mm, v(-5657.98, 515.98) * mm]});
            skFitSpline(sketch, "E282", {"points": [v(-5657.98, 515.98) * mm, v(-5662.09, 520.08) * mm, v(-5657.67, 523.52) * mm, v(-5648.17, 523.62) * mm]});
            skFitSpline(sketch, "E283", {"points": [v(-5647.8, 534.51) * mm, v(-5658.43, 541.24) * mm, v(-5612.67, 548.46) * mm, v(-5524.39, 553.98) * mm]});
            skFitSpline(sketch, "E284", {"points": [v(-5524.39, 553.98) * mm, v(-5447.22, 558.8) * mm, v(-5377.93, 566.55) * mm, v(-5370.4, 571.2) * mm]});
            skFitSpline(sketch, "E285", {"points": [v(-5370.4, 571.2) * mm, v(-5362.89, 575.84) * mm, v(-5351.85, 605.76) * mm, v(-5345.9, 637.67) * mm]});
            skLineSegment(sketch, "E286", {"start": v(-5468.09, 277.53) * mm, "end": v(-5322.48, 364.6) * mm});
            skLineSegment(sketch, "E287", {"start": v(-5322.48, 364.6) * mm, "end": v(-5337.81, 416.59) * mm});
            skLineSegment(sketch, "E288", {"start": v(-5337.81, 416.59) * mm, "end": v(-5353.15, 468.57) * mm});
            skLineSegment(sketch, "E289", {"start": v(-5353.15, 468.57) * mm, "end": v(-5501.84, 488.54) * mm});
            skFitSpline(sketch, "E290", {"points": [v(-5397.63, 722.96) * mm, v(-5432.05, 737.95) * mm, v(-5491.67, 763.66) * mm, v(-5530.1, 780.08) * mm]});
            skFitSpline(sketch, "E291", {"points": [v(-5530.1, 780.08) * mm, v(-5601.18, 810.45) * mm, v(-5622.73, 840.64) * mm, v(-5572.99, 840.17) * mm]});
            skFitSpline(sketch, "E292", {"points": [v(-5572.99, 840.17) * mm, v(-5557.9, 840.01) * mm, v(-5496.46, 829.05) * mm, v(-5436.45, 815.78) * mm]});
            skFitSpline(sketch, "E293", {"points": [v(-5436.45, 815.78) * mm, v(-5376.44, 802.52) * mm, v(-5320.93, 791.66) * mm, v(-5313.1, 791.66) * mm]});
            skFitSpline(sketch, "E294", {"points": [v(-5313.1, 791.66) * mm, v(-5305.27, 791.66) * mm, v(-5285, 812.6) * mm, v(-5268.06, 838.2) * mm]});
            skLineSegment(sketch, "E295", {"start": v(-5345.9, 637.67) * mm, "end": v(-5335.05, 695.7) * mm});
            skLineSegment(sketch, "E296", {"start": v(-5335.05, 695.7) * mm, "end": v(-5397.63, 722.96) * mm});
            skFitSpline(sketch, "E297", {"points": [v(-5309.12, 966.92) * mm, v(-5348.63, 1012.12) * mm, v(-5380.97, 1054.27) * mm, v(-5380.97, 1060.59) * mm]});
            skFitSpline(sketch, "E298", {"points": [v(-5380.97, 1060.59) * mm, v(-5380.97, 1085.42) * mm, v(-5344.5, 1069.4) * mm, v(-5266.4, 1010.29) * mm]});
            skFitSpline(sketch, "E299", {"points": [v(-5266.4, 1010.29) * mm, v(-5221.5, 976.3) * mm, v(-5180.92, 950.33) * mm, v(-5176.2, 952.57) * mm]});
            skFitSpline(sketch, "E300", {"points": [v(-5176.2, 952.57) * mm, v(-5132.5, 973.28) * mm, v(-5076.17, 1016.67) * mm, v(-5076.17, 1029.6) * mm]});
            skFitSpline(sketch, "E301", {"points": [v(-5076.17, 1029.6) * mm, v(-5076.17, 1038.44) * mm, v(-5087.14, 1071.27) * mm, v(-5100.55, 1102.56) * mm]});
            skFitSpline(sketch, "E302", {"points": [v(-5100.55, 1102.56) * mm, v(-5149.87, 1217.61) * mm, v(-5116.79, 1228.45) * mm, v(-5046.98, 1120.1) * mm]});
            skFitSpline(sketch, "E303", {"points": [v(-5046.98, 1120.1) * mm, v(-5011.85, 1065.58) * mm, v(-4994.42, 1048.5) * mm, v(-4979.93, 1054.36) * mm]});
            skFitSpline(sketch, "E304", {"points": [v(-4979.93, 1054.36) * mm, v(-4969.15, 1058.72) * mm, v(-4940.38, 1065.13) * mm, v(-4915.99, 1068.6) * mm]});
            skFitSpline(sketch, "E305", {"points": [v(-4915.99, 1068.6) * mm, v(-4876.07, 1074.3) * mm, v(-4870.9, 1079.35) * mm, v(-4864.3, 1119.22) * mm]});
            skFitSpline(sketch, "E306", {"points": [v(-4864.3, 1119.22) * mm, v(-4860.27, 1143.58) * mm, v(-4856.2, 1188.2) * mm, v(-4855.24, 1218.38) * mm]});
            skLineSegment(sketch, "E307", {"start": v(-5268.06, 838.2) * mm, "end": v(-5237.27, 884.74) * mm});
            skLineSegment(sketch, "E308", {"start": v(-5237.27, 884.74) * mm, "end": v(-5309.12, 966.92) * mm});
            skFitSpline(sketch, "E309", {"points": [v(-4832.6, 1230.57) * mm, v(-4830.3, 1264.01) * mm, v(-4825.27, 1252.17) * mm, v(-4809.35, 1175.87) * mm]});
            skLineSegment(sketch, "E310", {"start": v(-4855.24, 1218.38) * mm, "end": v(-4853.5, 1273.25) * mm});
            skLineSegment(sketch, "E311", {"start": v(-4853.5, 1273.25) * mm, "end": v(-4844.52, 1230.57) * mm});
            skLineSegment(sketch, "E312", {"start": v(-4844.52, 1230.57) * mm, "end": v(-4835.53, 1187.9) * mm});
            skLineSegment(sketch, "E313", {"start": v(-4835.53, 1187.9) * mm, "end": v(-4832.6, 1230.57) * mm});
            skFitSpline(sketch, "E314", {"points": [v(-4743.75, 1071.13) * mm, v(-4693.92, 1063.03) * mm, v(-4689.43, 1067.1) * mm, v(-4638.77, 1166.57) * mm]});
            skFitSpline(sketch, "E315", {"points": [v(-4638.77, 1166.57) * mm, v(-4624.25, 1195.06) * mm, v(-4604.26, 1218.38) * mm, v(-4594.33, 1218.38) * mm]});
            skFitSpline(sketch, "E316", {"points": [v(-4594.33, 1218.38) * mm, v(-4571.49, 1218.38) * mm, v(-4571.63, 1216.03) * mm, v(-4600.38, 1121.48) * mm]});
            skFitSpline(sketch, "E317", {"points": [v(-4600.38, 1121.48) * mm, v(-4613.53, 1078.24) * mm, v(-4623.1, 1042.13) * mm, v(-4621.63, 1041.24) * mm]});
            skFitSpline(sketch, "E318", {"points": [v(-4621.63, 1041.24) * mm, v(-4620.16, 1040.35) * mm, v(-4593.81, 1025.87) * mm, v(-4563.07, 1009.07) * mm]});
            skLineSegment(sketch, "E319", {"start": v(-4809.35, 1175.87) * mm, "end": v(-4789.02, 1078.49) * mm});
            skLineSegment(sketch, "E320", {"start": v(-4789.02, 1078.49) * mm, "end": v(-4743.75, 1071.13) * mm});
            skFitSpline(sketch, "E321", {"points": [v(-4441.15, 1037.1) * mm, v(-4333.97, 1132.2) * mm, v(-4311.55, 1113.23) * mm, v(-4398.15, 1000.7) * mm]});
            skLineSegment(sketch, "E322", {"start": v(-4563.07, 1009.07) * mm, "end": v(-4507.17, 978.5) * mm});
            skLineSegment(sketch, "E323", {"start": v(-4507.17, 978.5) * mm, "end": v(-4441.15, 1037.1) * mm});
            skFitSpline(sketch, "E324", {"points": [v(-4423.7, 898.65) * mm, v(-4408.31, 880.78) * mm, v(-4387.8, 854.82) * mm, v(-4378.1, 840.96) * mm]});
            skFitSpline(sketch, "E325", {"points": [v(-4378.1, 840.96) * mm, v(-4361.76, 817.65) * mm, v(-4357.38, 817.04) * mm, v(-4319.02, 832.74) * mm]});
            skFitSpline(sketch, "E326", {"points": [v(-4319.02, 832.74) * mm, v(-4239.53, 865.28) * mm, v(-4222.72, 867.86) * mm, v(-4222.72, 847.5) * mm]});
            skFitSpline(sketch, "E327", {"points": [v(-4222.72, 847.5) * mm, v(-4222.72, 837.07) * mm, v(-4246.04, 814.02) * mm, v(-4274.54, 796.27) * mm]});
            skFitSpline(sketch, "E328", {"points": [v(-4274.54, 796.27) * mm, v(-4303.04, 778.52) * mm, v(-4327.53, 763.1) * mm, v(-4328.96, 762.02) * mm]});
            skFitSpline(sketch, "E329", {"points": [v(-4328.96, 762.02) * mm, v(-4330.39, 760.93) * mm, v(-4323.53, 733.37) * mm, v(-4313.72, 700.76) * mm]});
            skFitSpline(sketch, "E330", {"points": [v(-4313.72, 700.76) * mm, v(-4303.9, 668.16) * mm, v(-4296.74, 613.55) * mm, v(-4297.8, 579.41) * mm]});
            skLineSegment(sketch, "E331", {"start": v(-4398.15, 1000.7) * mm, "end": v(-4451.65, 931.16) * mm});
            skLineSegment(sketch, "E332", {"start": v(-4451.65, 931.16) * mm, "end": v(-4423.7, 898.65) * mm});
            skFitSpline(sketch, "E333", {"points": [v(-4308.07, 578.3) * mm, v(-4315.56, 632.89) * mm, v(-4316.77, 634.8) * mm, v(-4319.68, 596.59) * mm]});
            skLineSegment(sketch, "E334", {"start": v(-4297.8, 579.41) * mm, "end": v(-4299.7, 517.34) * mm});
            skLineSegment(sketch, "E335", {"start": v(-4299.7, 517.34) * mm, "end": v(-4308.07, 578.3) * mm});
            skFitSpline(sketch, "E336", {"points": [v(-4332.83, 603.82) * mm, v(-4371.12, 796.99) * mm, v(-4541.95, 952.1) * mm, v(-4736.4, 970.25) * mm]});
            skFitSpline(sketch, "E337", {"points": [v(-4736.4, 970.25) * mm, v(-4884.25, 984.05) * mm, v(-5050.5, 909.3) * mm, v(-5136.75, 790.25) * mm]});
            skFitSpline(sketch, "E338", {"points": [v(-5136.75, 790.25) * mm, v(-5271.28, 604.53) * mm, v(-5244.35, 341.69) * mm, v(-5075.2, 189.6) * mm]});
            skFitSpline(sketch, "E339", {"points": [v(-5075.2, 189.6) * mm, v(-4988.2, 111.39) * mm, v(-4900.5, 79.5) * mm, v(-4771.37, 79.15) * mm]});
            skFitSpline(sketch, "E340", {"points": [v(-4771.37, 79.15) * mm, v(-4680.04, 78.9) * mm, v(-4657.99, 83.46) * mm, v(-4585.69, 117.52) * mm]});
            skFitSpline(sketch, "E341", {"points": [v(-4585.69, 117.52) * mm, v(-4505.83, 155.13) * mm, v(-4470.08, 155.4) * mm, v(-4512.57, 118.06) * mm]});
            skFitSpline(sketch, "E342", {"points": [v(-4512.57, 118.06) * mm, v(-4541.96, 92.23) * mm, v(-4621.49, 53.55) * mm, v(-4682.97, 35.19) * mm]});
            skFitSpline(sketch, "E343", {"points": [v(-4682.97, 35.19) * mm, v(-4711.47, 26.67) * mm, v(-4734.79, 12.56) * mm, v(-4734.79, 3.83) * mm]});
            skFitSpline(sketch, "E344", {"points": [v(-4734.79, 3.83) * mm, v(-4734.79, -19.84) * mm, v(-4758.96, -257.2) * mm, v(-4765.79, -300.54) * mm]});
            skFitSpline(sketch, "E345", {"points": [v(-4765.79, -300.54) * mm, v(-4769.04, -321.21) * mm, v(-4778.92, -338.13) * mm, v(-4787.74, -338.13) * mm]});
            skFitSpline(sketch, "E346", {"points": [v(-4787.74, -338.13) * mm, v(-4799.1, -338.13) * mm, v(-4809.95, -291.59) * mm, v(-4824.94, -178.62) * mm]});
            skLineSegment(sketch, "E347", {"start": v(-4319.68, 596.59) * mm, "end": v(-4322.93, 553.92) * mm});
            skLineSegment(sketch, "E348", {"start": v(-4322.93, 553.92) * mm, "end": v(-4332.83, 603.82) * mm});
            skFitSpline(sketch, "E349", {"points": [v(-4796.71, 47.95) * mm, v(-4822.62, 47.95) * mm, v(-4833.02, 42.96) * mm, v(-4828.99, 32.45) * mm]});
            skFitSpline(sketch, "E350", {"points": [v(-4828.99, 32.45) * mm, v(-4825.71, 23.93) * mm, v(-4815.8, -35.05) * mm, v(-4806.97, -98.61) * mm]});
            skFitSpline(sketch, "E351", {"points": [v(-4806.97, -98.61) * mm, v(-4792.41, -203.25) * mm, v(-4790.12, -209.57) * mm, v(-4782.7, -165.41) * mm]});
            skFitSpline(sketch, "E352", {"points": [v(-4782.7, -165.41) * mm, v(-4778.2, -138.59) * mm, v(-4770.92, -79.6) * mm, v(-4766.5, -34.35) * mm]});
            skLineSegment(sketch, "E353", {"start": v(-4766.5, -34.35) * mm, "end": v(-4758.5, 47.95) * mm});
            skLineSegment(sketch, "E354", {"start": v(-4758.5, 47.95) * mm, "end": v(-4796.71, 47.95) * mm});
            skFitSpline(sketch, "E355", {"points": [v(-4913.7, 54.85) * mm, v(-4875.06, 48.03) * mm, v(-4875.07, 48.05) * mm, v(-4918.34, 64.8) * mm]});
            skFitSpline(sketch, "E356", {"points": [v(-4918.34, 64.8) * mm, v(-5103.5, 136.55) * mm, v(-5214.76, 264.23) * mm, v(-5247.66, 442.77) * mm]});
            skFitSpline(sketch, "E357", {"points": [v(-5247.66, 442.77) * mm, v(-5285.52, 648.19) * mm, v(-5168.88, 868.93) * mm, v(-4975.86, 957.15) * mm]});
            skFitSpline(sketch, "E358", {"points": [v(-4975.86, 957.15) * mm, v(-4835.13, 1021.48) * mm, v(-4647.39, 1010.85) * mm, v(-4525.77, 931.68) * mm]});
            skFitSpline(sketch, "E359", {"points": [v(-4475.85, 931.44) * mm, v(-4471.82, 952.53) * mm, v(-4474.96, 958.36) * mm, v(-4487.7, 953.48) * mm]});
            skFitSpline(sketch, "E360", {"points": [v(-4487.7, 953.48) * mm, v(-4497.22, 949.82) * mm, v(-4537.5, 962.66) * mm, v(-4577.2, 982.02) * mm]});
            skFitSpline(sketch, "E361", {"points": [v(-4577.2, 982.02) * mm, v(-4635.97, 1010.67) * mm, v(-4649.4, 1022.75) * mm, v(-4649.42, 1046.98) * mm]});
            skFitSpline(sketch, "E362", {"points": [v(-4649.42, 1046.98) * mm, v(-4649.44, 1074.18) * mm, v(-4650.79, 1074.9) * mm, v(-4665.08, 1055.35) * mm]});
            skFitSpline(sketch, "E363", {"points": [v(-4665.08, 1055.35) * mm, v(-4687.89, 1024.16) * mm, v(-4805.85, 1039.92) * mm, v(-4819.17, 1075.93) * mm]});
            skFitSpline(sketch, "E364", {"points": [v(-4819.17, 1075.93) * mm, v(-4828.26, 1100.49) * mm, v(-4828.43, 1100.5) * mm, v(-4834.7, 1076.51) * mm]});
            skFitSpline(sketch, "E365", {"points": [v(-4834.7, 1076.51) * mm, v(-4839.71, 1057.34) * mm, v(-4859.32, 1048.81) * mm, v(-4928.36, 1035.78) * mm]});
            skFitSpline(sketch, "E366", {"points": [v(-4928.36, 1035.78) * mm, v(-5010.53, 1020.28) * mm, v(-5016.68, 1020.67) * mm, v(-5032.58, 1042.41) * mm]});
            skFitSpline(sketch, "E367", {"points": [v(-5032.58, 1042.41) * mm, v(-5048.42, 1064.07) * mm, v(-5049.1, 1063.58) * mm, v(-5043.56, 1034.6) * mm]});
            skFitSpline(sketch, "E368", {"points": [v(-5043.56, 1034.6) * mm, v(-5038.48, 1008.02) * mm, v(-5047.2, 997.33) * mm, v(-5105.49, 958.62) * mm]});
            skFitSpline(sketch, "E369", {"points": [v(-5105.49, 958.62) * mm, v(-5142.8, 933.85) * mm, v(-5177.65, 913.58) * mm, v(-5182.93, 913.58) * mm]});
            skFitSpline(sketch, "E370", {"points": [v(-5182.93, 913.58) * mm, v(-5188.2, 913.58) * mm, v(-5214.35, 931.31) * mm, v(-5241.03, 952.98) * mm]});
            skLineSegment(sketch, "E371", {"start": v(-4525.77, 931.68) * mm, "end": v(-4481.34, 902.75) * mm});
            skLineSegment(sketch, "E372", {"start": v(-4481.34, 902.75) * mm, "end": v(-4475.85, 931.44) * mm});
            skFitSpline(sketch, "E373", {"points": [v(-5249.9, 946.46) * mm, v(-5228.1, 921.2) * mm, v(-5210.28, 892.78) * mm, v(-5210.28, 883.29) * mm]});
            skFitSpline(sketch, "E374", {"points": [v(-5210.28, 883.29) * mm, v(-5210.28, 863.48) * mm, v(-5280.96, 754.87) * mm, v(-5293.44, 755.51) * mm]});
            skFitSpline(sketch, "E375", {"points": [v(-5293.44, 755.51) * mm, v(-5298, 755.75) * mm, v(-5337.33, 763.57) * mm, v(-5380.85, 772.9) * mm]});
            skFitSpline(sketch, "E376", {"points": [v(-5380.85, 772.9) * mm, v(-5424.37, 782.23) * mm, v(-5461.2, 788.65) * mm, v(-5462.67, 787.17) * mm]});
            skFitSpline(sketch, "E377", {"points": [v(-5462.67, 787.17) * mm, v(-5464.15, 785.7) * mm, v(-5429.72, 768.95) * mm, v(-5386.15, 749.98) * mm]});
            skLineSegment(sketch, "E378", {"start": v(-5241.03, 952.98) * mm, "end": v(-5289.52, 992.38) * mm});
            skLineSegment(sketch, "E379", {"start": v(-5289.52, 992.38) * mm, "end": v(-5249.9, 946.46) * mm});
            skFitSpline(sketch, "E380", {"points": [v(-5315.06, 640.79) * mm, v(-5319.53, 599.72) * mm, v(-5328.62, 559.25) * mm, v(-5335.28, 550.87) * mm]});
            skFitSpline(sketch, "E381", {"points": [v(-5335.28, 550.87) * mm, v(-5342.18, 542.18) * mm, v(-5374.66, 535.63) * mm, v(-5410.9, 535.63) * mm]});
            skFitSpline(sketch, "E382", {"points": [v(-5410.9, 535.63) * mm, v(-5504.75, 535.63) * mm, v(-5504.66, 519.1) * mm, v(-5410.73, 505.15) * mm]});
            skLineSegment(sketch, "E383", {"start": v(-5386.15, 749.98) * mm, "end": v(-5306.95, 715.47) * mm});
            skLineSegment(sketch, "E384", {"start": v(-5306.95, 715.47) * mm, "end": v(-5315.06, 640.79) * mm});
            skFitSpline(sketch, "E385", {"points": [v(-5312.33, 438.1) * mm, v(-5303.34, 407.92) * mm, v(-5295.91, 374.77) * mm, v(-5295.8, 364.43) * mm]});
            skFitSpline(sketch, "E386", {"points": [v(-5295.8, 364.43) * mm, v(-5295.71, 354.05) * mm, v(-5331.39, 324.7) * mm, v(-5375.43, 298.94) * mm]});
            skFitSpline(sketch, "E387", {"points": [v(-5375.43, 298.94) * mm, v(-5419.32, 273.27) * mm, v(-5453.14, 250.17) * mm, v(-5450.58, 247.6) * mm]});
            skFitSpline(sketch, "E388", {"points": [v(-5450.58, 247.6) * mm, v(-5448.02, 245.05) * mm, v(-5414, 253.95) * mm, v(-5374.96, 267.37) * mm]});
            skFitSpline(sketch, "E389", {"points": [v(-5374.96, 267.37) * mm, v(-5335.93, 280.8) * mm, v(-5292.51, 291.72) * mm, v(-5278.47, 291.64) * mm]});
            skFitSpline(sketch, "E390", {"points": [v(-5278.47, 291.64) * mm, v(-5252.78, 291.49) * mm, v(-5198.09, 222.82) * mm, v(-5198.09, 190.7) * mm]});
            skFitSpline(sketch, "E391", {"points": [v(-5198.09, 190.7) * mm, v(-5198.09, 181.85) * mm, v(-5228.82, 137.36) * mm, v(-5266.37, 91.83) * mm]});
            skLineSegment(sketch, "E392", {"start": v(-5410.73, 505.15) * mm, "end": v(-5328.66, 492.96) * mm});
            skLineSegment(sketch, "E393", {"start": v(-5328.66, 492.96) * mm, "end": v(-5312.33, 438.1) * mm});
            skFitSpline(sketch, "E394", {"points": [v(-5083.45, 120.7) * mm, v(-5045.91, 99.53) * mm, v(-5015.2, 78.5) * mm, v(-5015.2, 73.97) * mm]});
            skFitSpline(sketch, "E395", {"points": [v(-5015.2, 73.97) * mm, v(-5015.2, 69.45) * mm, v(-5026.41, 24.71) * mm, v(-5040.11, -25.45) * mm]});
            skFitSpline(sketch, "E396", {"points": [v(-5040.11, -25.45) * mm, v(-5053.8, -75.6) * mm, v(-5067.87, -127.61) * mm, v(-5071.36, -141.03) * mm]});
            skFitSpline(sketch, "E397", {"points": [v(-5071.36, -141.03) * mm, v(-5074.84, -154.44) * mm, v(-5049.5, -114.32) * mm, v(-5015.05, -51.87) * mm]});
            skFitSpline(sketch, "E398", {"points": [v(-5015.05, -51.87) * mm, v(-4953.5, 59.71) * mm, v(-4951.74, 61.56) * mm, v(-4913.7, 54.85) * mm]});
            skLineSegment(sketch, "E399", {"start": v(-5266.37, 91.83) * mm, "end": v(-5334.66, 9.05) * mm});
            skLineSegment(sketch, "E400", {"start": v(-5334.66, 9.05) * mm, "end": v(-5243.17, 84.13) * mm});
            skLineSegment(sketch, "E401", {"start": v(-5243.17, 84.13) * mm, "end": v(-5151.68, 159.22) * mm});
            skLineSegment(sketch, "E402", {"start": v(-5151.68, 159.22) * mm, "end": v(-5083.45, 120.7) * mm});
            skFitSpline(sketch, "E403", {"points": [v(-4503.14, 140.25) * mm, v(-4503.14, 143.6) * mm, v(-4514.11, 140.47) * mm, v(-4527.52, 133.3) * mm]});
            skFitSpline(sketch, "E404", {"points": [v(-4527.52, 133.3) * mm, v(-4540.94, 126.12) * mm, v(-4551.9, 117.5) * mm, v(-4551.9, 114.15) * mm]});
            skFitSpline(sketch, "E405", {"points": [v(-4551.9, 114.15) * mm, v(-4551.9, 110.8) * mm, v(-4540.94, 113.93) * mm, v(-4527.52, 121.1) * mm]});
            skFitSpline(sketch, "E406", {"points": [v(-4527.52, 121.1) * mm, v(-4514.11, 128.28) * mm, v(-4503.14, 136.9) * mm, v(-4503.14, 140.25) * mm]});
            skLineSegment(sketch, "E407", {"start": v(-4913.7, 54.85) * mm, "end": v(-4913.7, 54.85) * mm});
            skFitSpline(sketch, "E408", {"points": [v(-4351.6, 778.08) * mm, v(-4347.92, 784.03) * mm, v(-4356.14, 791.83) * mm, v(-4369.86, 795.41) * mm]});
            skFitSpline(sketch, "E409", {"points": [v(-4369.86, 795.41) * mm, v(-4390.32, 800.76) * mm, v(-4392.22, 798.82) * mm, v(-4380.42, 784.6) * mm]});
            skFitSpline(sketch, "E410", {"points": [v(-4380.42, 784.6) * mm, v(-4363.59, 764.32) * mm, v(-4360.53, 763.63) * mm, v(-4351.6, 778.08) * mm]});
            skFitSpline(sketch, "E411", {"points": [v(-4411.18, -62.87) * mm, v(-4432.05, -19.2) * mm, v(-4442.36, 17.7) * mm, v(-4437.35, 30.76) * mm]});
            skFitSpline(sketch, "E412", {"points": [v(-4437.35, 30.76) * mm, v(-4430.37, 48.96) * mm, v(-4418.72, 42.08) * mm, v(-4362.48, -13.46) * mm]});
            skFitSpline(sketch, "E413", {"points": [v(-4362.48, -13.46) * mm, v(-4290.38, -84.66) * mm, v(-4283.18, -102.9) * mm, v(-4319.46, -122.3) * mm]});
            skFitSpline(sketch, "E414", {"points": [v(-4319.46, -122.3) * mm, v(-4362.02, -145.09) * mm, v(-4376.3, -135.83) * mm, v(-4411.18, -62.87) * mm]});
            skFitSpline(sketch, "E415", {"points": [v(-4320.26, -93.35) * mm, v(-4320.26, -92.03) * mm, v(-4340.08, -72.04) * mm, v(-4364.3, -48.93) * mm]});
            skFitSpline(sketch, "E416", {"points": [v(-4382.55, -58.33) * mm, v(-4364.73, -93.84) * mm, v(-4351.1, -107.58) * mm, v(-4338.5, -102.75) * mm]});
            skFitSpline(sketch, "E417", {"points": [v(-4338.5, -102.75) * mm, v(-4328.47, -98.9) * mm, v(-4320.26, -94.67) * mm, v(-4320.26, -93.35) * mm]});
            skLineSegment(sketch, "E418", {"start": v(-4364.3, -48.93) * mm, "end": v(-4408.36, -6.91) * mm});
            skLineSegment(sketch, "E419", {"start": v(-4408.36, -6.91) * mm, "end": v(-4382.55, -58.33) * mm});
            skFitSpline(sketch, "E420", {"points": [v(-6605, -83.11) * mm, v(-6609.2, -61.32) * mm, v(-6616.04, 47.84) * mm, v(-6620.23, 159.46) * mm]});
            skFitSpline(sketch, "E421", {"points": [v(-6513.42, 369.82) * mm, v(-6287.11, 384.45) * mm, v(-5450.66, 414.31) * mm, v(-5444.33, 407.99) * mm]});
            skFitSpline(sketch, "E422", {"points": [v(-5444.33, 407.99) * mm, v(-5440.77, 404.43) * mm, v(-5445.63, 401.43) * mm, v(-5455.13, 401.33) * mm]});
            skFitSpline(sketch, "E423", {"points": [v(-5455.13, 401.33) * mm, v(-5466.97, 401.2) * mm, v(-5468.04, 398.33) * mm, v(-5458.53, 392.19) * mm]});
            skFitSpline(sketch, "E424", {"points": [v(-5458.53, 392.19) * mm, v(-5445.62, 383.86) * mm, v(-6552.47, -122.76) * mm, v(-6583.54, -122.74) * mm]});
            skFitSpline(sketch, "E425", {"points": [v(-6583.54, -122.74) * mm, v(-6591.16, -122.74) * mm, v(-6600.82, -104.9) * mm, v(-6605, -83.11) * mm]});
            skLineSegment(sketch, "E426", {"start": v(-6620.23, 159.46) * mm, "end": v(-6627.85, 362.42) * mm});
            skLineSegment(sketch, "E427", {"start": v(-6627.85, 362.42) * mm, "end": v(-6513.42, 369.82) * mm});
            skFitSpline(sketch, "E428", {"points": [v(-5702.12, 295.39) * mm, v(-5593.77, 343.7) * mm, v(-5506.54, 384.7) * mm, v(-5508.29, 386.5) * mm]});
            skFitSpline(sketch, "E429", {"points": [v(-5508.29, 386.5) * mm, v(-5512.89, 391.25) * mm, v(-6513.77, 352.35) * mm, v(-6558.97, 345.67) * mm]});
            skFitSpline(sketch, "E430", {"points": [v(-6558.97, 345.67) * mm, v(-6592.77, 340.67) * mm, v(-6597.74, 334.67) * mm, v(-6603.48, 291.94) * mm]});
            skFitSpline(sketch, "E431", {"points": [v(-6603.48, 291.94) * mm, v(-6610.03, 243.1) * mm, v(-6596.18, 24.85) * mm, v(-6581.6, -52.84) * mm]});
            skFitSpline(sketch, "E432", {"points": [v(-6236.37, 56.08) * mm, v(-6050.89, 139.38) * mm, v(-5810.47, 247.08) * mm, v(-5702.12, 295.39) * mm]});
            skLineSegment(sketch, "E433", {"start": v(-6581.6, -52.84) * mm, "end": v(-6573.62, -95.4) * mm});
            skLineSegment(sketch, "E434", {"start": v(-6573.62, -95.4) * mm, "end": v(-6236.37, 56.08) * mm});
            skFitSpline(sketch, "E435", {"points": [v(2808.5, -54.15) * mm, v(2803.75, -49.4) * mm, v(2799.87, 131.87) * mm, v(2799.87, 348.69) * mm]});
            skFitSpline(sketch, "E436", {"points": [v(2896.89, -59.23) * mm, v(2853.02, -61.18) * mm, v(2813.24, -58.9) * mm, v(2808.5, -54.15) * mm]});
            skLineSegment(sketch, "E437", {"start": v(2799.87, 348.69) * mm, "end": v(2799.87, 742.9) * mm});
            skLineSegment(sketch, "E438", {"start": v(2799.87, 742.9) * mm, "end": v(2586.5, 742.9) * mm});
            skLineSegment(sketch, "E439", {"start": v(2586.5, 742.9) * mm, "end": v(2373.15, 742.9) * mm});
            skLineSegment(sketch, "E440", {"start": v(2373.15, 742.9) * mm, "end": v(2373.15, 822.27) * mm});
            skLineSegment(sketch, "E441", {"start": v(2373.15, 822.27) * mm, "end": v(2373.15, 901.65) * mm});
            skLineSegment(sketch, "E442", {"start": v(2373.15, 901.65) * mm, "end": v(2888.26, 898.47) * mm});
            skLineSegment(sketch, "E443", {"start": v(2888.26, 898.47) * mm, "end": v(3403.37, 895.3) * mm});
            skLineSegment(sketch, "E444", {"start": v(3403.37, 895.3) * mm, "end": v(3403.37, 822.14) * mm});
            skLineSegment(sketch, "E445", {"start": v(3403.37, 822.14) * mm, "end": v(3403.37, 748.99) * mm});
            skLineSegment(sketch, "E446", {"start": v(3403.37, 748.99) * mm, "end": v(3193.23, 745.65) * mm});
            skLineSegment(sketch, "E447", {"start": v(3193.23, 745.65) * mm, "end": v(2983.08, 742.32) * mm});
            skLineSegment(sketch, "E448", {"start": v(2983.08, 742.32) * mm, "end": v(2979.87, 343.32) * mm});
            skLineSegment(sketch, "E449", {"start": v(2979.87, 343.32) * mm, "end": v(2976.65, -55.68) * mm});
            skLineSegment(sketch, "E450", {"start": v(2976.65, -55.68) * mm, "end": v(2896.89, -59.23) * mm});
            skFitSpline(sketch, "E451", {"points": [v(2946.17, 351.75) * mm, v(2946.17, 559.08) * mm, v(2949.5, 737.39) * mm, v(2953.57, 748) * mm]});
            skFitSpline(sketch, "E452", {"points": [v(2953.57, 748) * mm, v(2959.92, 764.53) * mm, v(2990.37, 767.28) * mm, v(3166.93, 767.28) * mm]});
            skFitSpline(sketch, "E453", {"points": [v(3603.31, -42.89) * mm, v(3533.58, -21.3) * mm, v(3439.1, 74.45) * mm, v(3427.84, 134.95) * mm]});
            skFitSpline(sketch, "E454", {"points": [v(3427.84, 134.95) * mm, v(3423.64, 157.5) * mm, v(3421.9, 299.9) * mm, v(3423.98, 451.37) * mm]});
            skLineSegment(sketch, "E455", {"start": v(3166.93, 767.28) * mm, "end": v(3372.9, 767.28) * mm});
            skLineSegment(sketch, "E456", {"start": v(3372.9, 767.28) * mm, "end": v(3372.9, 822.14) * mm});
            skLineSegment(sketch, "E457", {"start": v(3372.9, 822.14) * mm, "end": v(3372.9, 877) * mm});
            skLineSegment(sketch, "E458", {"start": v(3372.9, 877) * mm, "end": v(2885.21, 877) * mm});
            skLineSegment(sketch, "E459", {"start": v(2885.21, 877) * mm, "end": v(2397.53, 877) * mm});
            skLineSegment(sketch, "E460", {"start": v(2397.53, 877) * mm, "end": v(2397.53, 822.43) * mm});
            skLineSegment(sketch, "E461", {"start": v(2397.53, 822.43) * mm, "end": v(2397.53, 767.85) * mm});
            skLineSegment(sketch, "E462", {"start": v(2397.53, 767.85) * mm, "end": v(2607.84, 764.52) * mm});
            skLineSegment(sketch, "E463", {"start": v(2607.84, 764.52) * mm, "end": v(2818.16, 761.18) * mm});
            skLineSegment(sketch, "E464", {"start": v(2818.16, 761.18) * mm, "end": v(2821.37, 367.99) * mm});
            skLineSegment(sketch, "E465", {"start": v(2821.37, 367.99) * mm, "end": v(2824.6, -25.2) * mm});
            skLineSegment(sketch, "E466", {"start": v(2824.6, -25.2) * mm, "end": v(2885.38, -25.2) * mm});
            skLineSegment(sketch, "E467", {"start": v(2885.38, -25.2) * mm, "end": v(2946.17, -25.2) * mm});
            skLineSegment(sketch, "E468", {"start": v(2946.17, -25.2) * mm, "end": v(2946.17, 351.75) * mm});
            skFitSpline(sketch, "E469", {"points": [v(3463.48, 778.27) * mm, v(3483.12, 806.6) * mm, v(3524.27, 844.52) * mm, v(3554.92, 862.54) * mm]});
            skLineSegment(sketch, "E470", {"start": v(3423.98, 451.37) * mm, "end": v(3427.76, 726.77) * mm});
            skLineSegment(sketch, "E471", {"start": v(3427.76, 726.77) * mm, "end": v(3463.48, 778.27) * mm});
            skFitSpline(sketch, "E472", {"points": [v(4045.5, 742.9) * mm, v(3571.88, 735.79) * mm, v(3604.54, 746.33) * mm, v(3604.54, 600.52) * mm]});
            skLineSegment(sketch, "E473", {"start": v(3554.92, 862.54) * mm, "end": v(3610.64, 895.3) * mm});
            skLineSegment(sketch, "E474", {"start": v(3610.64, 895.3) * mm, "end": v(4031.26, 895.3) * mm});
            skLineSegment(sketch, "E475", {"start": v(4031.26, 895.3) * mm, "end": v(4451.88, 895.3) * mm});
            skLineSegment(sketch, "E476", {"start": v(4451.88, 895.3) * mm, "end": v(4451.88, 822.14) * mm});
            skLineSegment(sketch, "E477", {"start": v(4451.88, 822.14) * mm, "end": v(4451.88, 748.99) * mm});
            skLineSegment(sketch, "E478", {"start": v(4451.88, 748.99) * mm, "end": v(4045.5, 742.9) * mm});
            skFitSpline(sketch, "E479", {"points": [v(3604.54, 251) * mm, v(3604.54, 168.24) * mm, v(3608.66, 145.53) * mm, v(3626.65, 129.26) * mm]});
            skFitSpline(sketch, "E480", {"points": [v(3626.65, 129.26) * mm, v(3646.04, 111.7) * mm, v(3698.07, 108.85) * mm, v(4050.32, 106.03) * mm]});
            skLineSegment(sketch, "E481", {"start": v(3604.54, 600.52) * mm, "end": v(3604.54, 511.58) * mm});
            skLineSegment(sketch, "E482", {"start": v(3604.54, 511.58) * mm, "end": v(4003.83, 508.36) * mm});
            skLineSegment(sketch, "E483", {"start": v(4003.83, 508.36) * mm, "end": v(4403.12, 505.15) * mm});
            skLineSegment(sketch, "E484", {"start": v(4403.12, 505.15) * mm, "end": v(4406.75, 428.95) * mm});
            skLineSegment(sketch, "E485", {"start": v(4406.75, 428.95) * mm, "end": v(4410.38, 352.75) * mm});
            skLineSegment(sketch, "E486", {"start": v(4410.38, 352.75) * mm, "end": v(4007.46, 352.75) * mm});
            skLineSegment(sketch, "E487", {"start": v(4007.46, 352.75) * mm, "end": v(3604.54, 352.75) * mm});
            skLineSegment(sketch, "E488", {"start": v(3604.54, 352.75) * mm, "end": v(3604.54, 251) * mm});
            skFitSpline(sketch, "E489", {"points": [v(4055.64, -57.97) * mm, v(3742.14, -59.77) * mm, v(3647.7, -56.62) * mm, v(3603.31, -42.89) * mm]});
            skLineSegment(sketch, "E490", {"start": v(4050.32, 106.03) * mm, "end": v(4451.88, 102.81) * mm});
            skLineSegment(sketch, "E491", {"start": v(4451.88, 102.81) * mm, "end": v(4451.88, 23.57) * mm});
            skLineSegment(sketch, "E492", {"start": v(4451.88, 23.57) * mm, "end": v(4451.88, -55.68) * mm});
            skLineSegment(sketch, "E493", {"start": v(4451.88, -55.68) * mm, "end": v(4055.64, -57.97) * mm});
            skFitSpline(sketch, "E494", {"points": [v(4019.76, 84.53) * mm, v(3541.5, 84.53) * mm, v(3580.16, 69.28) * mm, v(3580.16, 257.93) * mm]});
            skLineSegment(sketch, "E495", {"start": v(4421.4, 29.66) * mm, "end": v(4421.4, 84.53) * mm});
            skLineSegment(sketch, "E496", {"start": v(4421.4, 84.53) * mm, "end": v(4019.76, 84.53) * mm});
            skFitSpline(sketch, "E497", {"points": [v(3580.16, 597.14) * mm, v(3580.16, 697.98) * mm, v(3582.72, 710) * mm, v(3610.08, 737.35) * mm]});
            skLineSegment(sketch, "E498", {"start": v(3580.16, 257.93) * mm, "end": v(3580.16, 377.13) * mm});
            skLineSegment(sketch, "E499", {"start": v(3580.16, 377.13) * mm, "end": v(3982.5, 377.13) * mm});
            skLineSegment(sketch, "E500", {"start": v(3982.5, 377.13) * mm, "end": v(4384.83, 377.13) * mm});
            skLineSegment(sketch, "E501", {"start": v(4384.83, 377.13) * mm, "end": v(4384.83, 432) * mm});
            skLineSegment(sketch, "E502", {"start": v(4384.83, 432) * mm, "end": v(4384.83, 486.86) * mm});
            skLineSegment(sketch, "E503", {"start": v(4384.83, 486.86) * mm, "end": v(3982.5, 486.86) * mm});
            skLineSegment(sketch, "E504", {"start": v(3982.5, 486.86) * mm, "end": v(3580.16, 486.86) * mm});
            skLineSegment(sketch, "E505", {"start": v(3580.16, 486.86) * mm, "end": v(3580.16, 597.14) * mm});
            skFitSpline(sketch, "E506", {"points": [v(4046.5, 876.93) * mm, v(3819.82, 876.9) * mm, v(3653.18, 871.75) * mm, v(3625.01, 863.93) * mm]});
            skFitSpline(sketch, "E507", {"points": [v(3625.01, 863.93) * mm, v(3562.5, 846.57) * mm, v(3488.53, 777.46) * mm, v(3464.16, 713.64) * mm]});
            skFitSpline(sketch, "E508", {"points": [v(3464.16, 713.64) * mm, v(3447.48, 669.98) * mm, v(3444.9, 619.04) * mm, v(3448.2, 398.44) * mm]});
            skLineSegment(sketch, "E509", {"start": v(3610.08, 737.35) * mm, "end": v(3640, 767.28) * mm});
            skLineSegment(sketch, "E510", {"start": v(3640, 767.28) * mm, "end": v(4030.7, 767.28) * mm});
            skLineSegment(sketch, "E511", {"start": v(4030.7, 767.28) * mm, "end": v(4421.4, 767.28) * mm});
            skLineSegment(sketch, "E512", {"start": v(4421.4, 767.28) * mm, "end": v(4421.4, 822.14) * mm});
            skLineSegment(sketch, "E513", {"start": v(4421.4, 822.14) * mm, "end": v(4421.4, 877) * mm});
            skLineSegment(sketch, "E514", {"start": v(4421.4, 877) * mm, "end": v(4046.5, 876.93) * mm});
            skFitSpline(sketch, "E515", {"points": [v(3488.72, 83.42) * mm, v(3508.83, 54.88) * mm, v(3549.47, 18.76) * mm, v(3579.03, 3.16) * mm]});
            skFitSpline(sketch, "E516", {"points": [v(3579.03, 3.16) * mm, v(3632.07, -24.85) * mm, v(3637.82, -25.21) * mm, v(4027.08, -25.21) * mm]});
            skLineSegment(sketch, "E517", {"start": v(3448.2, 398.44) * mm, "end": v(3452.14, 135.31) * mm});
            skLineSegment(sketch, "E518", {"start": v(3452.14, 135.31) * mm, "end": v(3488.72, 83.42) * mm});
            skFitSpline(sketch, "E519", {"points": [v(4662.3, -44.52) * mm, v(4599.1, -21.84) * mm, v(4562.23, 4.13) * mm, v(4527.04, 50.75) * mm]});
            skFitSpline(sketch, "E520", {"points": [v(4527.04, 50.75) * mm, v(4474.25, 120.66) * mm, v(4467.68, 168.6) * mm, v(4472.23, 450.51) * mm]});
            skFitSpline(sketch, "E521", {"points": [v(4472.23, 450.51) * mm, v(4476.97, 744.38) * mm, v(4479.98, 756.41) * mm, v(4567.3, 831.15) * mm]});
            skFitSpline(sketch, "E522", {"points": [v(4567.3, 831.15) * mm, v(4645.52, 898.1) * mm, v(4670.83, 901.39) * mm, v(5108.62, 901.39) * mm]});
            skLineSegment(sketch, "E523", {"start": v(4027.08, -25.21) * mm, "end": v(4421.4, -25.21) * mm});
            skLineSegment(sketch, "E524", {"start": v(4421.4, -25.21) * mm, "end": v(4421.4, 29.65) * mm});
            skLineSegment(sketch, "E525", {"start": v(4421.4, 29.65) * mm, "end": v(4421.4, 29.66) * mm});
            skFitSpline(sketch, "E526", {"points": [v(4655.44, 415.45) * mm, v(4658.27, 212) * mm, v(4663.1, 144.42) * mm, v(4675.88, 129.04) * mm]});
            skFitSpline(sketch, "E527", {"points": [v(4675.88, 129.04) * mm, v(4690.82, 111.06) * mm, v(4736.2, 108.9) * mm, v(5100.11, 108.9) * mm]});
            skLineSegment(sketch, "E528", {"start": v(5108.62, 901.39) * mm, "end": v(5506.5, 901.39) * mm});
            skLineSegment(sketch, "E529", {"start": v(5506.5, 901.39) * mm, "end": v(5506.5, 822.14) * mm});
            skLineSegment(sketch, "E530", {"start": v(5506.5, 822.14) * mm, "end": v(5506.5, 742.9) * mm});
            skLineSegment(sketch, "E531", {"start": v(5506.5, 742.9) * mm, "end": v(5109.7, 742.9) * mm});
            skLineSegment(sketch, "E532", {"start": v(5109.7, 742.9) * mm, "end": v(4712.9, 742.9) * mm});
            skLineSegment(sketch, "E533", {"start": v(4712.9, 742.9) * mm, "end": v(4682.32, 712.3) * mm});
            skLineSegment(sketch, "E534", {"start": v(4682.32, 712.3) * mm, "end": v(4651.73, 681.72) * mm});
            skLineSegment(sketch, "E535", {"start": v(4651.73, 681.72) * mm, "end": v(4655.44, 415.45) * mm});
            skFitSpline(sketch, "E536", {"points": [v(5104.16, -58.28) * mm, v(4798.08, -60.29) * mm, v(4697.54, -57.16) * mm, v(4662.3, -44.52) * mm]});
            skLineSegment(sketch, "E537", {"start": v(5100.11, 108.9) * mm, "end": v(5507.6, 108.9) * mm});
            skLineSegment(sketch, "E538", {"start": v(5507.6, 108.9) * mm, "end": v(5504, 26.61) * mm});
            skLineSegment(sketch, "E539", {"start": v(5504, 26.61) * mm, "end": v(5500.4, -55.68) * mm});
            skLineSegment(sketch, "E540", {"start": v(5500.4, -55.68) * mm, "end": v(5104.16, -58.28) * mm});
            skFitSpline(sketch, "E541", {"points": [v(4653.94, 116.65) * mm, v(4630.12, 146.93) * mm, v(4628.67, 164.12) * mm, v(4628.67, 415.96) * mm]});
            skFitSpline(sketch, "E542", {"points": [v(4628.67, 415.96) * mm, v(4628.67, 694.34) * mm, v(4636.25, 741.35) * mm, v(4684.08, 759.7) * mm]});
            skFitSpline(sketch, "E543", {"points": [v(4684.08, 759.7) * mm, v(4694.93, 763.87) * mm, v(4878.93, 767.28) * mm, v(5092.96, 767.28) * mm]});
            skLineSegment(sketch, "E544", {"start": v(5482.1, 29.66) * mm, "end": v(5482.1, 84.53) * mm});
            skLineSegment(sketch, "E545", {"start": v(5482.1, 84.53) * mm, "end": v(5080.66, 84.53) * mm});
            skLineSegment(sketch, "E546", {"start": v(5080.66, 84.53) * mm, "end": v(4679.2, 84.53) * mm});
            skLineSegment(sketch, "E547", {"start": v(4679.2, 84.53) * mm, "end": v(4653.94, 116.65) * mm});
            skFitSpline(sketch, "E548", {"points": [v(5082.82, 874.43) * mm, v(4706.39, 871.11) * mm, v(4680.78, 869.47) * mm, v(4635.41, 845.67) * mm]});
            skFitSpline(sketch, "E549", {"points": [v(4635.41, 845.67) * mm, v(4608.95, 831.78) * mm, v(4570.54, 799.74) * mm, v(4550.07, 774.46) * mm]});
            skLineSegment(sketch, "E550", {"start": v(5092.96, 767.28) * mm, "end": v(5482.1, 767.28) * mm});
            skLineSegment(sketch, "E551", {"start": v(5482.1, 767.28) * mm, "end": v(5482.1, 822.62) * mm});
            skLineSegment(sketch, "E552", {"start": v(5482.1, 822.62) * mm, "end": v(5482.1, 877.95) * mm});
            skLineSegment(sketch, "E553", {"start": v(5482.1, 877.95) * mm, "end": v(5082.82, 874.43) * mm});
            skFitSpline(sketch, "E554", {"points": [v(4508.96, 452.23) * mm, v(4506.6, 284.2) * mm, v(4510.06, 159.11) * mm, v(4517.78, 132.95) * mm]});
            skFitSpline(sketch, "E555", {"points": [v(4517.78, 132.95) * mm, v(4524.77, 109.29) * mm, v(4548.47, 72.59) * mm, v(4570.44, 51.4) * mm]});
            skFitSpline(sketch, "E556", {"points": [v(4570.44, 51.4) * mm, v(4650.59, -25.93) * mm, v(4644.64, -25.04) * mm, v(5082.82, -25.13) * mm]});
            skLineSegment(sketch, "E557", {"start": v(4550.07, 774.46) * mm, "end": v(4512.84, 728.5) * mm});
            skLineSegment(sketch, "E558", {"start": v(4512.84, 728.5) * mm, "end": v(4508.96, 452.23) * mm});
            skLineSegment(sketch, "E559", {"start": v(5082.82, -25.13) * mm, "end": v(5482.1, -25.2) * mm});
            skLineSegment(sketch, "E560", {"start": v(5482.1, -25.2) * mm, "end": v(5482.1, 29.66) * mm});
            skLineSegment(sketch, "E561", {"start": v(5543.07, 419.8) * mm, "end": v(5543.07, 901.39) * mm});
            skLineSegment(sketch, "E562", {"start": v(5543.07, 901.39) * mm, "end": v(5628.41, 901.39) * mm});
            skLineSegment(sketch, "E563", {"start": v(5628.41, 901.39) * mm, "end": v(5713.76, 901.39) * mm});
            skLineSegment(sketch, "E564", {"start": v(5713.76, 901.39) * mm, "end": v(5713.76, 706.32) * mm});
            skLineSegment(sketch, "E565", {"start": v(5713.76, 706.32) * mm, "end": v(5713.76, 511.25) * mm});
            skLineSegment(sketch, "E566", {"start": v(5713.76, 511.25) * mm, "end": v(6055.13, 511.25) * mm});
            skLineSegment(sketch, "E567", {"start": v(6055.13, 511.25) * mm, "end": v(6396.5, 511.25) * mm});
            skLineSegment(sketch, "E568", {"start": v(6396.5, 511.25) * mm, "end": v(6396.5, 706.32) * mm});
            skLineSegment(sketch, "E569", {"start": v(6396.5, 706.32) * mm, "end": v(6396.5, 901.39) * mm});
            skLineSegment(sketch, "E570", {"start": v(6396.5, 901.39) * mm, "end": v(6481.85, 901.39) * mm});
            skLineSegment(sketch, "E571", {"start": v(6481.85, 901.39) * mm, "end": v(6567.2, 901.39) * mm});
            skLineSegment(sketch, "E572", {"start": v(6567.2, 901.39) * mm, "end": v(6567.2, 419.8) * mm});
            skLineSegment(sketch, "E573", {"start": v(6567.2, 419.8) * mm, "end": v(6567.2, -61.78) * mm});
            skLineSegment(sketch, "E574", {"start": v(6567.2, -61.78) * mm, "end": v(6482.15, -61.78) * mm});
            skLineSegment(sketch, "E575", {"start": v(6482.15, -61.78) * mm, "end": v(6397.1, -61.78) * mm});
            skLineSegment(sketch, "E576", {"start": v(6397.1, -61.78) * mm, "end": v(6393.76, 142.44) * mm});
            skLineSegment(sketch, "E577", {"start": v(6393.76, 142.44) * mm, "end": v(6390.41, 346.65) * mm});
            skLineSegment(sketch, "E578", {"start": v(6390.41, 346.65) * mm, "end": v(6055.13, 346.65) * mm});
            skLineSegment(sketch, "E579", {"start": v(6055.13, 346.65) * mm, "end": v(5719.85, 346.65) * mm});
            skLineSegment(sketch, "E580", {"start": v(5719.85, 346.65) * mm, "end": v(5716.5, 142.44) * mm});
            skLineSegment(sketch, "E581", {"start": v(5716.5, 142.44) * mm, "end": v(5713.17, -61.78) * mm});
            skLineSegment(sketch, "E582", {"start": v(5713.17, -61.78) * mm, "end": v(5628.12, -61.78) * mm});
            skLineSegment(sketch, "E583", {"start": v(5628.12, -61.78) * mm, "end": v(5543.07, -61.78) * mm});
            skLineSegment(sketch, "E584", {"start": v(5543.07, -61.78) * mm, "end": v(5543.07, 419.8) * mm});
            skFitSpline(sketch, "E585", {"points": [v(-3393.67, 304.37) * mm, v(-3393.67, 596.8) * mm, v(-3390.38, 666.21) * mm, v(-3374.73, 703.66) * mm]});
            skFitSpline(sketch, "E586", {"points": [v(-3374.73, 703.66) * mm, v(-3350.82, 760.92) * mm, v(-3302.97, 811.63) * mm, v(-3244.47, 841.71) * mm]});
            skFitSpline(sketch, "E587", {"points": [v(-3244.47, 841.71) * mm, v(-3201.85, 863.64) * mm, v(-3173.19, 864.94) * mm, v(-2799.47, 861.93) * mm]});
            skLineSegment(sketch, "E588", {"start": v(5692.12, 172.92) * mm, "end": v(5695.47, 371.04) * mm});
            skLineSegment(sketch, "E589", {"start": v(5695.47, 371.04) * mm, "end": v(6055.13, 371.04) * mm});
            skLineSegment(sketch, "E590", {"start": v(6055.13, 371.04) * mm, "end": v(6414.8, 371.04) * mm});
            skLineSegment(sketch, "E591", {"start": v(6414.8, 371.04) * mm, "end": v(6418.15, 172.92) * mm});
            skLineSegment(sketch, "E592", {"start": v(6418.15, 172.92) * mm, "end": v(6421.5, -25.2) * mm});
            skLineSegment(sketch, "E593", {"start": v(6421.5, -25.2) * mm, "end": v(6482.15, -25.2) * mm});
            skLineSegment(sketch, "E594", {"start": v(6482.15, -25.2) * mm, "end": v(6542.81, -25.2) * mm});
            skLineSegment(sketch, "E595", {"start": v(6542.81, -25.2) * mm, "end": v(6542.81, 425.9) * mm});
            skLineSegment(sketch, "E596", {"start": v(6542.81, 425.9) * mm, "end": v(6542.81, 877) * mm});
            skLineSegment(sketch, "E597", {"start": v(6542.81, 877) * mm, "end": v(6482.16, 877) * mm});
            skLineSegment(sketch, "E598", {"start": v(6482.16, 877) * mm, "end": v(6421.51, 877) * mm});
            skLineSegment(sketch, "E599", {"start": v(6421.51, 877) * mm, "end": v(6418.15, 684.98) * mm});
            skLineSegment(sketch, "E600", {"start": v(6418.15, 684.98) * mm, "end": v(6414.8, 492.96) * mm});
            skLineSegment(sketch, "E601", {"start": v(6414.8, 492.96) * mm, "end": v(6055.13, 492.96) * mm});
            skLineSegment(sketch, "E602", {"start": v(6055.13, 492.96) * mm, "end": v(5695.47, 492.96) * mm});
            skLineSegment(sketch, "E603", {"start": v(5695.47, 492.96) * mm, "end": v(5692.11, 684.98) * mm});
            skLineSegment(sketch, "E604", {"start": v(5692.11, 684.98) * mm, "end": v(5688.75, 877) * mm});
            skLineSegment(sketch, "E605", {"start": v(5688.75, 877) * mm, "end": v(5628.1, 877) * mm});
            skLineSegment(sketch, "E606", {"start": v(5628.1, 877) * mm, "end": v(5567.45, 877) * mm});
            skLineSegment(sketch, "E607", {"start": v(5567.45, 877) * mm, "end": v(5567.45, 425.9) * mm});
            skLineSegment(sketch, "E608", {"start": v(5567.45, 425.9) * mm, "end": v(5567.45, -25.2) * mm});
            skLineSegment(sketch, "E609", {"start": v(5567.45, -25.2) * mm, "end": v(5628.11, -25.2) * mm});
            skLineSegment(sketch, "E610", {"start": v(5628.11, -25.2) * mm, "end": v(5688.77, -25.2) * mm});
            skLineSegment(sketch, "E611", {"start": v(5688.77, -25.2) * mm, "end": v(5692.12, 172.92) * mm});
            skFitSpline(sketch, "E612", {"points": [v(-3200.2, 683) * mm, v(-3219.47, 659.19) * mm, v(-3223.33, 638.28) * mm, v(-3220.44, 573.27) * mm]});
            skLineSegment(sketch, "E613", {"start": v(-2799.47, 861.93) * mm, "end": v(-2400.02, 858.72) * mm});
            skLineSegment(sketch, "E614", {"start": v(-2400.02, 858.72) * mm, "end": v(-2400.02, 791.66) * mm});
            skLineSegment(sketch, "E615", {"start": v(-2400.02, 791.66) * mm, "end": v(-2400.02, 724.6) * mm});
            skLineSegment(sketch, "E616", {"start": v(-2400.02, 724.6) * mm, "end": v(-2788.2, 718.5) * mm});
            skLineSegment(sketch, "E617", {"start": v(-2788.2, 718.5) * mm, "end": v(-3176.4, 712.41) * mm});
            skLineSegment(sketch, "E618", {"start": v(-3176.4, 712.41) * mm, "end": v(-3200.2, 683) * mm});
            skLineSegment(sketch, "E619", {"start": v(-3220.44, 573.27) * mm, "end": v(-3216.88, 492.96) * mm});
            skLineSegment(sketch, "E620", {"start": v(-3216.88, 492.96) * mm, "end": v(-2908.43, 489.7) * mm});
            skLineSegment(sketch, "E621", {"start": v(-2908.43, 489.7) * mm, "end": v(-2599.98, 486.44) * mm});
            skLineSegment(sketch, "E622", {"start": v(-2599.98, 486.44) * mm, "end": v(-2603.63, 416.55) * mm});
            skLineSegment(sketch, "E623", {"start": v(-2603.63, 416.55) * mm, "end": v(-2607.28, 346.65) * mm});
            skLineSegment(sketch, "E624", {"start": v(-2607.28, 346.65) * mm, "end": v(-2915.13, 343.4) * mm});
            skLineSegment(sketch, "E625", {"start": v(-2915.13, 343.4) * mm, "end": v(-3222.98, 340.14) * mm});
            skLineSegment(sketch, "E626", {"start": v(-3222.98, 340.14) * mm, "end": v(-3222.98, 145.28) * mm});
            skLineSegment(sketch, "E627", {"start": v(-3222.98, 145.28) * mm, "end": v(-3222.98, -49.59) * mm});
            skLineSegment(sketch, "E628", {"start": v(-3222.98, -49.59) * mm, "end": v(-3308.32, -49.59) * mm});
            skLineSegment(sketch, "E629", {"start": v(-3308.32, -49.59) * mm, "end": v(-3393.67, -49.59) * mm});
            skLineSegment(sketch, "E630", {"start": v(-3393.67, -49.59) * mm, "end": v(-3393.67, 304.37) * mm});
            skFitSpline(sketch, "E631", {"points": [v(-3247.36, 570.77) * mm, v(-3247.36, 648.95) * mm, v(-3242.77, 672.3) * mm, v(-3222.23, 698.4) * mm]});
            skLineSegment(sketch, "E632", {"start": v(-3244.62, 160.73) * mm, "end": v(-3241.27, 358.85) * mm});
            skLineSegment(sketch, "E633", {"start": v(-3241.27, 358.85) * mm, "end": v(-2932.73, 362.1) * mm});
            skLineSegment(sketch, "E634", {"start": v(-2932.73, 362.1) * mm, "end": v(-2624.2, 365.36) * mm});
            skLineSegment(sketch, "E635", {"start": v(-2624.2, 365.36) * mm, "end": v(-2627.93, 416.97) * mm});
            skLineSegment(sketch, "E636", {"start": v(-2627.93, 416.97) * mm, "end": v(-2631.67, 468.57) * mm});
            skLineSegment(sketch, "E637", {"start": v(-2631.67, 468.57) * mm, "end": v(-2939.52, 471.83) * mm});
            skLineSegment(sketch, "E638", {"start": v(-2939.52, 471.83) * mm, "end": v(-3247.36, 475.09) * mm});
            skLineSegment(sketch, "E639", {"start": v(-3247.36, 475.09) * mm, "end": v(-3247.36, 570.77) * mm});
            skFitSpline(sketch, "E640", {"points": [v(-2800.86, 840.43) * mm, v(-3041.94, 840.43) * mm, v(-3197.59, 835.61) * mm, v(-3219.14, 827.5) * mm]});
            skFitSpline(sketch, "E641", {"points": [v(-3219.14, 827.5) * mm, v(-3265.69, 809.94) * mm, v(-3331.93, 745.38) * mm, v(-3352.45, 697.57) * mm]});
            skFitSpline(sketch, "E642", {"points": [v(-3352.45, 697.57) * mm, v(-3365.46, 667.25) * mm, v(-3369.28, 579.26) * mm, v(-3369.28, 310.47) * mm]});
            skLineSegment(sketch, "E643", {"start": v(-3222.23, 698.4) * mm, "end": v(-3197.1, 730.36) * mm});
            skLineSegment(sketch, "E644", {"start": v(-3197.1, 730.36) * mm, "end": v(-2810.75, 733.58) * mm});
            skLineSegment(sketch, "E645", {"start": v(-2810.75, 733.58) * mm, "end": v(-2424.4, 736.8) * mm});
            skLineSegment(sketch, "E646", {"start": v(-2424.4, 736.8) * mm, "end": v(-2420.66, 788.61) * mm});
            skLineSegment(sketch, "E647", {"start": v(-2420.66, 788.61) * mm, "end": v(-2416.9, 840.43) * mm});
            skLineSegment(sketch, "E648", {"start": v(-2416.9, 840.43) * mm, "end": v(-2800.86, 840.43) * mm});
            skFitSpline(sketch, "E649", {"points": [v(-2252.56, -21.95) * mm, v(-2278.74, -6.98) * mm, v(-2317.15, 26.35) * mm, v(-2337.9, 52.1) * mm]});
            skLineSegment(sketch, "E650", {"start": v(-3369.28, 310.47) * mm, "end": v(-3369.28, -37.4) * mm});
            skLineSegment(sketch, "E651", {"start": v(-3369.28, -37.4) * mm, "end": v(-3308.63, -37.4) * mm});
            skLineSegment(sketch, "E652", {"start": v(-3308.63, -37.4) * mm, "end": v(-3247.97, -37.4) * mm});
            skLineSegment(sketch, "E653", {"start": v(-3247.97, -37.4) * mm, "end": v(-3244.62, 160.73) * mm});
            skFitSpline(sketch, "E654", {"points": [v(-2378.82, 393.48) * mm, v(-2381.91, 680.3) * mm, v(-2381.27, 689.3) * mm, v(-2354.33, 736.3) * mm]});
            skFitSpline(sketch, "E655", {"points": [v(-2354.33, 736.3) * mm, v(-2339.11, 762.83) * mm, v(-2302.92, 801.24) * mm, v(-2273.9, 821.63) * mm]});
            skLineSegment(sketch, "E656", {"start": v(-2337.9, 52.1) * mm, "end": v(-2375.64, 98.92) * mm});
            skLineSegment(sketch, "E657", {"start": v(-2375.64, 98.92) * mm, "end": v(-2378.82, 393.48) * mm});
            skFitSpline(sketch, "E658", {"points": [v(-1510, 825.35) * mm, v(-1483.18, 807) * mm, v(-1447.52, 771.74) * mm, v(-1430.76, 747) * mm]});
            skFitSpline(sketch, "E659", {"points": [v(-1430.76, 747) * mm, v(-1400.32, 702.07) * mm, v(-1400.28, 701.58) * mm, v(-1400.28, 406.5) * mm]});
            skLineSegment(sketch, "E660", {"start": v(-2273.9, 821.63) * mm, "end": v(-2221.14, 858.72) * mm});
            skLineSegment(sketch, "E661", {"start": v(-2221.14, 858.72) * mm, "end": v(-1889.95, 858.72) * mm});
            skLineSegment(sketch, "E662", {"start": v(-1889.95, 858.72) * mm, "end": v(-1558.77, 858.72) * mm});
            skLineSegment(sketch, "E663", {"start": v(-1558.77, 858.72) * mm, "end": v(-1510, 825.35) * mm});
            skFitSpline(sketch, "E664", {"points": [v(-1436.85, 59.08) * mm, v(-1456.97, 30.52) * mm, v(-1497.6, -5.62) * mm, v(-1527.16, -21.22) * mm]});
            skFitSpline(sketch, "E665", {"points": [v(-1527.16, -21.22) * mm, v(-1579.4, -48.8) * mm, v(-1589.62, -49.58) * mm, v(-1892.92, -49.39) * mm]});
            skFitSpline(sketch, "E666", {"points": [v(-1892.92, -49.39) * mm, v(-2193.3, -49.2) * mm, v(-2206.73, -48.17) * mm, v(-2252.56, -21.95) * mm]});
            skLineSegment(sketch, "E667", {"start": v(-1400.28, 406.5) * mm, "end": v(-1400.28, 111.01) * mm});
            skLineSegment(sketch, "E668", {"start": v(-1400.28, 111.01) * mm, "end": v(-1436.85, 59.08) * mm});
            skFitSpline(sketch, "E669", {"points": [v(-1548.82, -2.39) * mm, v(-1511.93, 15.77) * mm, v(-1477.94, 44.9) * mm, v(-1457.38, 75.97) * mm]});
            skFitSpline(sketch, "E670", {"points": [v(-1457.38, 739.26) * mm, v(-1477.1, 769.05) * mm, v(-1511.35, 799) * mm, v(-1543.53, 814.57) * mm]});
            skFitSpline(sketch, "E671", {"points": [v(-1543.53, 814.57) * mm, v(-1593.46, 838.74) * mm, v(-1616.25, 840.43) * mm, v(-1892.3, 840.43) * mm]});
            skFitSpline(sketch, "E672", {"points": [v(-1892.3, 840.43) * mm, v(-2163.11, 840.43) * mm, v(-2191.58, 838.42) * mm, v(-2235.2, 816.16) * mm]});
            skFitSpline(sketch, "E673", {"points": [v(-2235.2, 816.16) * mm, v(-2292.66, 786.85) * mm, v(-2338.09, 729.53) * mm, v(-2356.08, 663.65) * mm]});
            skFitSpline(sketch, "E674", {"points": [v(-2356.08, 663.65) * mm, v(-2376.61, 588.48) * mm, v(-2373.36, 211.53) * mm, v(-2351.54, 138.06) * mm]});
            skFitSpline(sketch, "E675", {"points": [v(-2351.54, 138.06) * mm, v(-2326.99, 55.39) * mm, v(-2262.53, -2.55) * mm, v(-2168.37, -26.58) * mm]});
            skFitSpline(sketch, "E676", {"points": [v(-2168.37, -26.58) * mm, v(-2148.26, -31.71) * mm, v(-2013.84, -34.87) * mm, v(-1869.67, -33.6) * mm]});
            skFitSpline(sketch, "E677", {"points": [v(-1869.67, -33.6) * mm, v(-1620.95, -31.42) * mm, v(-1604.54, -29.82) * mm, v(-1548.82, -2.39) * mm]});
            skLineSegment(sketch, "E678", {"start": v(-1457.38, 75.97) * mm, "end": v(-1424.66, 125.42) * mm});
            skLineSegment(sketch, "E679", {"start": v(-1424.66, 125.42) * mm, "end": v(-1424.66, 407.61) * mm});
            skLineSegment(sketch, "E680", {"start": v(-1424.66, 407.61) * mm, "end": v(-1424.66, 689.81) * mm});
            skLineSegment(sketch, "E681", {"start": v(-1424.66, 689.81) * mm, "end": v(-1457.38, 739.26) * mm});
            skFitSpline(sketch, "E682", {"points": [v(-2174.47, 80.98) * mm, v(-2234.54, 103.07) * mm, v(-2235.43, 107.71) * mm, v(-2235.43, 400.7) * mm]});
            skFitSpline(sketch, "E683", {"points": [v(-2235.43, 400.7) * mm, v(-2235.43, 630.6) * mm, v(-2232.27, 681.02) * mm, v(-2216.45, 703.6) * mm]});
            skFitSpline(sketch, "E684", {"points": [v(-2216.45, 703.6) * mm, v(-2197.7, 730.37) * mm, v(-2193.8, 730.7) * mm, v(-1896.4, 730.52) * mm]});
            skFitSpline(sketch, "E685", {"points": [v(-1896.4, 730.52) * mm, v(-1730.83, 730.42) * mm, v(-1589.31, 726.3) * mm, v(-1581.93, 721.37) * mm]});
            skFitSpline(sketch, "E686", {"points": [v(-1581.93, 721.37) * mm, v(-1546.35, 697.61) * mm, v(-1540.48, 653.24) * mm, v(-1540.48, 407.8) * mm]});
            skFitSpline(sketch, "E687", {"points": [v(-1540.48, 407.8) * mm, v(-1540.48, 136.44) * mm, v(-1548.52, 95.01) * mm, v(-1604, 80.15) * mm]});
            skFitSpline(sketch, "E688", {"points": [v(-1604, 80.15) * mm, v(-1638.42, 70.93) * mm, v(-2149.16, 71.68) * mm, v(-2174.47, 80.98) * mm]});
            skFitSpline(sketch, "E689", {"points": [v(-1584.05, 127.2) * mm, v(-1569, 147.14) * mm, v(-1565.64, 198.2) * mm, v(-1565.64, 407.61) * mm]});
            skFitSpline(sketch, "E690", {"points": [v(-1565.64, 407.61) * mm, v(-1565.64, 617.04) * mm, v(-1569, 668.08) * mm, v(-1584.05, 688.03) * mm]});
            skFitSpline(sketch, "E691", {"points": [v(-1584.05, 688.03) * mm, v(-1601.36, 710.96) * mm, v(-1619.03, 712.63) * mm, v(-1880.25, 716.08) * mm]});
            skFitSpline(sketch, "E692", {"points": [v(-1880.25, 716.08) * mm, v(-2141.14, 719.53) * mm, v(-2159.84, 718.3) * mm, v(-2187.59, 695.83) * mm]});
            skFitSpline(sketch, "E693", {"points": [v(-2187.59, 119.4) * mm, v(-2159.84, 96.93) * mm, v(-2141.14, 95.7) * mm, v(-1880.25, 99.14) * mm]});
            skFitSpline(sketch, "E694", {"points": [v(-1880.25, 99.14) * mm, v(-1619.03, 102.6) * mm, v(-1601.36, 104.27) * mm, v(-1584.05, 127.2) * mm]});
            skLineSegment(sketch, "E695", {"start": v(-2187.59, 695.83) * mm, "end": v(-2217.14, 671.9) * mm});
            skLineSegment(sketch, "E696", {"start": v(-2217.14, 671.9) * mm, "end": v(-2217.14, 407.61) * mm});
            skLineSegment(sketch, "E697", {"start": v(-2217.14, 407.61) * mm, "end": v(-2217.14, 143.33) * mm});
            skLineSegment(sketch, "E698", {"start": v(-2217.14, 143.33) * mm, "end": v(-2187.59, 119.4) * mm});
            skFitSpline(sketch, "E699", {"points": [v(-473.68, 825.35) * mm, v(-398.23, 773.73) * mm, v(-365.78, 716.8) * mm, v(-359.99, 625.88) * mm]});
            skFitSpline(sketch, "E700", {"points": [v(-359.99, 625.88) * mm, v(-353, 516.2) * mm, v(-364.05, 473.87) * mm, v(-415.27, 414.04) * mm]});
            skFitSpline(sketch, "E701", {"points": [v(-415.27, 414.04) * mm, v(-468.58, 351.76) * mm, v(-539.1, 316.8) * mm, v(-612.22, 316.44) * mm]});
            skLineSegment(sketch, "E702", {"start": v(-1345.41, 408.08) * mm, "end": v(-1345.41, 865.74) * mm});
            skLineSegment(sketch, "E703", {"start": v(-1345.41, 865.74) * mm, "end": v(-933.93, 862.23) * mm});
            skLineSegment(sketch, "E704", {"start": v(-933.93, 862.23) * mm, "end": v(-522.45, 858.72) * mm});
            skLineSegment(sketch, "E705", {"start": v(-522.45, 858.72) * mm, "end": v(-473.68, 825.35) * mm});
            skFitSpline(sketch, "E706", {"points": [v(-499.44, 144.69) * mm, v(-408.16, 50.37) * mm, v(-333.48, -31.92) * mm, v(-333.48, -38.2) * mm]});
            skFitSpline(sketch, "E707", {"points": [v(-333.48, -38.2) * mm, v(-333.48, -44.46) * mm, v(-379.12, -49.59) * mm, v(-434.92, -49.59) * mm]});
            skLineSegment(sketch, "E708", {"start": v(-612.22, 316.44) * mm, "end": v(-665.4, 316.17) * mm});
            skLineSegment(sketch, "E709", {"start": v(-665.4, 316.17) * mm, "end": v(-499.44, 144.69) * mm});
            skLineSegment(sketch, "E710", {"start": v(-434.92, -49.59) * mm, "end": v(-536.36, -49.59) * mm});
            skLineSegment(sketch, "E711", {"start": v(-536.36, -49.59) * mm, "end": v(-710.22, 133.3) * mm});
            skLineSegment(sketch, "E712", {"start": v(-710.22, 133.3) * mm, "end": v(-884.08, 316.17) * mm});
            skLineSegment(sketch, "E713", {"start": v(-884.08, 316.17) * mm, "end": v(-1029.4, 316.17) * mm});
            skLineSegment(sketch, "E714", {"start": v(-1029.4, 316.17) * mm, "end": v(-1174.72, 316.17) * mm});
            skLineSegment(sketch, "E715", {"start": v(-1174.72, 316.17) * mm, "end": v(-1174.72, 133.3) * mm});
            skLineSegment(sketch, "E716", {"start": v(-1174.72, 133.3) * mm, "end": v(-1174.72, -49.59) * mm});
            skLineSegment(sketch, "E717", {"start": v(-1174.72, -49.59) * mm, "end": v(-1260.07, -49.59) * mm});
            skLineSegment(sketch, "E718", {"start": v(-1260.07, -49.59) * mm, "end": v(-1345.41, -49.59) * mm});
            skLineSegment(sketch, "E719", {"start": v(-1345.41, -49.59) * mm, "end": v(-1345.41, 408.07) * mm});
            skLineSegment(sketch, "E720", {"start": v(-1345.41, 408.07) * mm, "end": v(-1345.41, 408.08) * mm});
            skFitSpline(sketch, "E721", {"points": [v(-524.82, 134.17) * mm, v(-617.4, 228.53) * mm, v(-694.91, 313.57) * mm, v(-697.08, 323.14) * mm]});
            skFitSpline(sketch, "E722", {"points": [v(-697.08, 323.14) * mm, v(-700.11, 336.52) * mm, v(-685.98, 340.62) * mm, v(-636.12, 340.83) * mm]});
            skFitSpline(sketch, "E723", {"points": [v(-636.12, 340.83) * mm, v(-555.24, 341.16) * mm, v(-485.28, 372.05) * mm, v(-434.56, 429.82) * mm]});
            skFitSpline(sketch, "E724", {"points": [v(-434.56, 429.82) * mm, v(-390.17, 480.38) * mm, v(-376.96, 532.67) * mm, v(-384.77, 626.9) * mm]});
            skFitSpline(sketch, "E725", {"points": [v(-384.77, 626.9) * mm, v(-391.86, 712.37) * mm, v(-436.07, 780.13) * mm, v(-507.2, 814.57) * mm]});
            skFitSpline(sketch, "E726", {"points": [v(-507.2, 814.57) * mm, v(-558.2, 839.24) * mm, v(-578.2, 840.42) * mm, v(-946.93, 840.42) * mm]});
            skLineSegment(sketch, "E727", {"start": v(-1201.84, 154.63) * mm, "end": v(-1198.47, 340.56) * mm});
            skLineSegment(sketch, "E728", {"start": v(-1198.47, 340.56) * mm, "end": v(-1035.72, 340.56) * mm});
            skLineSegment(sketch, "E729", {"start": v(-1035.72, 340.56) * mm, "end": v(-872.96, 340.56) * mm});
            skLineSegment(sketch, "E730", {"start": v(-872.96, 340.56) * mm, "end": v(-691.61, 151.56) * mm});
            skLineSegment(sketch, "E731", {"start": v(-691.61, 151.56) * mm, "end": v(-510.26, -37.43) * mm});
            skLineSegment(sketch, "E732", {"start": v(-510.26, -37.43) * mm, "end": v(-433.38, -37.41) * mm});
            skLineSegment(sketch, "E733", {"start": v(-433.38, -37.41) * mm, "end": v(-356.5, -37.4) * mm});
            skLineSegment(sketch, "E734", {"start": v(-356.5, -37.4) * mm, "end": v(-524.82, 134.17) * mm});
            skFitSpline(sketch, "E735", {"points": [v(-1333.22, 409.64) * mm, v(-1333.22, 172.7) * mm, v(-1329.3, -25.06) * mm, v(-1324.53, -29.84) * mm]});
            skFitSpline(sketch, "E736", {"points": [v(-1324.53, -29.84) * mm, v(-1319.75, -34.62) * mm, v(-1290.95, -36.9) * mm, v(-1260.52, -34.92) * mm]});
            skLineSegment(sketch, "E737", {"start": v(-946.93, 840.42) * mm, "end": v(-1333.22, 840.42) * mm});
            skLineSegment(sketch, "E738", {"start": v(-1333.22, 840.42) * mm, "end": v(-1333.22, 409.64) * mm});
            skLineSegment(sketch, "E739", {"start": v(-1260.52, -34.92) * mm, "end": v(-1205.2, -31.3) * mm});
            skLineSegment(sketch, "E740", {"start": v(-1205.2, -31.3) * mm, "end": v(-1201.84, 154.63) * mm});
            skFitSpline(sketch, "E741", {"points": [v(-879.07, 730.51) * mm, v(-703.05, 730.42) * mm, v(-553, 726.3) * mm, v(-545.61, 721.37) * mm]});
            skFitSpline(sketch, "E742", {"points": [v(-545.61, 721.37) * mm, v(-497.46, 689.22) * mm, v(-487.1, 536.22) * mm, v(-529.43, 482.4) * mm]});
            skLineSegment(sketch, "E743", {"start": v(-1199.1, 590.5) * mm, "end": v(-1199.1, 730.7) * mm});
            skLineSegment(sketch, "E744", {"start": v(-1199.1, 730.7) * mm, "end": v(-879.07, 730.51) * mm});
            skFitSpline(sketch, "E745", {"points": [v(-547.53, 501.77) * mm, v(-522.68, 537.24) * mm, v(-522.81, 655.02) * mm, v(-547.73, 688.03) * mm]});
            skFitSpline(sketch, "E746", {"points": [v(-547.73, 688.03) * mm, v(-565.14, 711.09) * mm, v(-582.69, 712.61) * mm, v(-870.43, 716.06) * mm]});
            skLineSegment(sketch, "E747", {"start": v(-529.43, 482.4) * mm, "end": v(-554.7, 450.28) * mm});
            skLineSegment(sketch, "E748", {"start": v(-554.7, 450.28) * mm, "end": v(-876.9, 450.28) * mm});
            skLineSegment(sketch, "E749", {"start": v(-876.9, 450.28) * mm, "end": v(-1199.1, 450.28) * mm});
            skLineSegment(sketch, "E750", {"start": v(-1199.1, 450.28) * mm, "end": v(-1199.1, 590.5) * mm});
            skFitSpline(sketch, "E751", {"points": [v(-870.62, 474.67) * mm, v(-570.18, 474.67) * mm, v(-566.28, 475) * mm, v(-547.53, 501.77) * mm]});
            skLineSegment(sketch, "E752", {"start": v(-870.43, 716.06) * mm, "end": v(-1174.73, 719.7) * mm});
            skLineSegment(sketch, "E753", {"start": v(-1174.73, 719.7) * mm, "end": v(-1174.73, 597.19) * mm});
            skLineSegment(sketch, "E754", {"start": v(-1174.73, 597.19) * mm, "end": v(-1174.73, 474.67) * mm});
            skLineSegment(sketch, "E755", {"start": v(-1174.73, 474.67) * mm, "end": v(-870.62, 474.67) * mm});
            skFitSpline(sketch, "E756", {"points": [v(-260.14, 380.18) * mm, v(-259.95, 822.34) * mm, v(-257.06, 851.54) * mm, v(-210.4, 880.65) * mm]});
            skFitSpline(sketch, "E757", {"points": [v(-210.4, 880.65) * mm, v(-174.85, 902.83) * mm, v(-131.75, 878.59) * mm, v(-69.12, 801.19) * mm]});
            skFitSpline(sketch, "E758", {"points": [v(-69.12, 801.19) * mm, v(-35.04, 759.07) * mm, v(88.9, 605.46) * mm, v(206.3, 459.85) * mm]});
            skFitSpline(sketch, "E759", {"points": [v(698.46, 536.53) * mm, v(976.97, 877.73) * mm, v(1009.56, 909.16) * mm, v(1055.25, 880.65) * mm]});
            skFitSpline(sketch, "E760", {"points": [v(1055.25, 880.65) * mm, v(1101.91, 851.54) * mm, v(1104.82, 822.34) * mm, v(1105, 380.18) * mm]});
            skLineSegment(sketch, "E761", {"start": v(206.3, 459.85) * mm, "end": v(419.76, 195.09) * mm});
            skLineSegment(sketch, "E762", {"start": v(419.76, 195.09) * mm, "end": v(698.46, 536.53) * mm});
            skFitSpline(sketch, "E763", {"points": [v(696.96, 235.13) * mm, v(469.98, -44.1) * mm, v(464.65, -49.59) * mm, v(420.05, -49.59) * mm]});
            skFitSpline(sketch, "E764", {"points": [v(420.05, -49.59) * mm, v(375.4, -49.59) * mm, v(370.4, -44.42) * mm, v(142.47, 237.94) * mm]});
            skLineSegment(sketch, "E765", {"start": v(1105, 380.18) * mm, "end": v(1105.17, -49.59) * mm});
            skLineSegment(sketch, "E766", {"start": v(1105.17, -49.59) * mm, "end": v(1020.05, -49.59) * mm});
            skLineSegment(sketch, "E767", {"start": v(1020.05, -49.59) * mm, "end": v(934.93, -49.59) * mm});
            skLineSegment(sketch, "E768", {"start": v(934.93, -49.59) * mm, "end": v(931.66, 235.13) * mm});
            skLineSegment(sketch, "E769", {"start": v(931.66, 235.13) * mm, "end": v(928.39, 519.84) * mm});
            skLineSegment(sketch, "E770", {"start": v(928.39, 519.84) * mm, "end": v(696.96, 235.13) * mm});
            skFitSpline(sketch, "E771", {"points": [v(-114.02, 253.9) * mm, v(-114.02, 481.54) * mm, v(-110.56, 546.54) * mm, v(-98.19, 551.29) * mm]});
            skFitSpline(sketch, "E772", {"points": [v(-98.19, 551.29) * mm, v(-88.5, 555) * mm, v(9.14, 444.25) * mm, v(153.25, 266.08) * mm]});
            skFitSpline(sketch, "E773", {"points": [v(153.25, 266.08) * mm, v(353.46, 18.54) * mm, v(393.66, -25.16) * mm, v(420.88, -24.94) * mm]});
            skFitSpline(sketch, "E774", {"points": [v(420.88, -24.94) * mm, v(447.86, -24.73) * mm, v(490.17, 21.24) * mm, v(689.28, 266.64) * mm]});
            skFitSpline(sketch, "E775", {"points": [v(689.28, 266.64) * mm, v(841.57, 454.32) * mm, v(931.57, 555.7) * mm, v(942.27, 551.59) * mm]});
            skFitSpline(sketch, "E776", {"points": [v(942.27, 551.59) * mm, v(955.64, 546.45) * mm, v(958.88, 488.51) * mm, v(958.88, 253.9) * mm]});
            skLineSegment(sketch, "E777", {"start": v(142.47, 237.94) * mm, "end": v(-89.64, 525.46) * mm});
            skLineSegment(sketch, "E778", {"start": v(-89.64, 525.46) * mm, "end": v(-89.64, 237.94) * mm});
            skLineSegment(sketch, "E779", {"start": v(-89.64, 237.94) * mm, "end": v(-89.64, -49.59) * mm});
            skLineSegment(sketch, "E780", {"start": v(-89.64, -49.59) * mm, "end": v(-174.98, -49.59) * mm});
            skLineSegment(sketch, "E781", {"start": v(-174.98, -49.59) * mm, "end": v(-260.32, -49.59) * mm});
            skLineSegment(sketch, "E782", {"start": v(-260.32, -49.59) * mm, "end": v(-260.15, 380.18) * mm});
            skLineSegment(sketch, "E783", {"start": v(-260.15, 380.18) * mm, "end": v(-260.14, 380.18) * mm});
            skFitSpline(sketch, "E784", {"points": [v(1080.8, 387.98) * mm, v(1080.8, 790.89) * mm, v(1079.55, 814.86) * mm, v(1057.15, 842.13) * mm]});
            skFitSpline(sketch, "E785", {"points": [v(1057.15, 842.13) * mm, v(1035.1, 868.97) * mm, v(1031.44, 869.68) * mm, v(1002.92, 852.62) * mm]});
            skFitSpline(sketch, "E786", {"points": [v(1002.92, 852.62) * mm, v(986.1, 842.56) * mm, v(850.82, 684.53) * mm, v(702.3, 501.43) * mm]});
            skFitSpline(sketch, "E787", {"points": [v(702.3, 501.43) * mm, v(553.8, 318.34) * mm, v(425.18, 170.2) * mm, v(416.5, 172.25) * mm]});
            skFitSpline(sketch, "E788", {"points": [v(416.5, 172.25) * mm, v(407.83, 174.3) * mm, v(276.12, 330.96) * mm, v(123.81, 520.39) * mm]});
            skFitSpline(sketch, "E789", {"points": [v(123.81, 520.39) * mm, v(-57.9, 746.4) * mm, v(-160.82, 864.81) * mm, v(-175.54, 864.81) * mm]});
            skFitSpline(sketch, "E790", {"points": [v(-175.54, 864.81) * mm, v(-187.88, 864.81) * mm, v(-206.52, 852.62) * mm, v(-216.96, 837.72) * mm]});
            skFitSpline(sketch, "E791", {"points": [v(-216.96, 837.72) * mm, v(-233.24, 814.48) * mm, v(-235.94, 751.41) * mm, v(-235.94, 394.74) * mm]});
            skFitSpline(sketch, "E792", {"points": [v(-235.94, 394.74) * mm, v(-235.94, 166) * mm, v(-232.28, -24.8) * mm, v(-227.81, -29.27) * mm]});
            skFitSpline(sketch, "E793", {"points": [v(-227.81, -29.27) * mm, v(-223.34, -33.74) * mm, v(-195.9, -37.4) * mm, v(-166.85, -37.4) * mm]});
            skLineSegment(sketch, "E794", {"start": v(958.88, 253.9) * mm, "end": v(958.88, -37.4) * mm});
            skLineSegment(sketch, "E795", {"start": v(958.88, -37.4) * mm, "end": v(1019.84, -37.4) * mm});
            skLineSegment(sketch, "E796", {"start": v(1019.84, -37.4) * mm, "end": v(1080.8, -37.4) * mm});
            skLineSegment(sketch, "E797", {"start": v(1080.8, -37.4) * mm, "end": v(1080.8, 387.98) * mm});
            skFitSpline(sketch, "E798", {"points": [v(1190.9, 191.2) * mm, v(1191.35, 480.46) * mm, v(1203.76, 589.04) * mm, v(1246.03, 673.6) * mm]});
            skFitSpline(sketch, "E799", {"points": [v(1246.03, 673.6) * mm, v(1299.5, 780.58) * mm, v(1372.12, 842.47) * mm, v(1489.84, 881.38) * mm]});
            skFitSpline(sketch, "E800", {"points": [v(1489.84, 881.38) * mm, v(1543.22, 899.02) * mm, v(1604.83, 901.3) * mm, v(1953.13, 898.51) * mm]});
            skLineSegment(sketch, "E801", {"start": v(-166.85, -37.4) * mm, "end": v(-114.02, -37.4) * mm});
            skLineSegment(sketch, "E802", {"start": v(-114.02, -37.4) * mm, "end": v(-114.02, 253.9) * mm});
            skLineSegment(sketch, "E803", {"start": v(1953.13, 898.51) * mm, "end": v(2354.86, 895.3) * mm});
            skLineSegment(sketch, "E804", {"start": v(2354.86, 895.3) * mm, "end": v(2358.05, 422.85) * mm});
            skLineSegment(sketch, "E805", {"start": v(2358.05, 422.85) * mm, "end": v(2361.24, -49.59) * mm});
            skLineSegment(sketch, "E806", {"start": v(2361.24, -49.59) * mm, "end": v(2269.66, -49.59) * mm});
            skLineSegment(sketch, "E807", {"start": v(2269.66, -49.59) * mm, "end": v(2178.08, -49.59) * mm});
            skLineSegment(sketch, "E808", {"start": v(2178.08, -49.59) * mm, "end": v(2178.08, 145.49) * mm});
            skLineSegment(sketch, "E809", {"start": v(2178.08, 145.49) * mm, "end": v(2178.08, 340.56) * mm});
            skLineSegment(sketch, "E810", {"start": v(2178.08, 340.56) * mm, "end": v(1775.74, 340.56) * mm});
            skLineSegment(sketch, "E811", {"start": v(1775.74, 340.56) * mm, "end": v(1373.4, 340.56) * mm});
            skLineSegment(sketch, "E812", {"start": v(1373.4, 340.56) * mm, "end": v(1373.4, 145.49) * mm});
            skLineSegment(sketch, "E813", {"start": v(1373.4, 145.49) * mm, "end": v(1373.4, -49.59) * mm});
            skLineSegment(sketch, "E814", {"start": v(1373.4, -49.59) * mm, "end": v(1281.96, -49.59) * mm});
            skLineSegment(sketch, "E815", {"start": v(1281.96, -49.59) * mm, "end": v(1190.52, -49.59) * mm});
            skLineSegment(sketch, "E816", {"start": v(1190.52, -49.59) * mm, "end": v(1190.9, 191.2) * mm});
            skLineSegment(sketch, "E817", {"start": v(1190.9, 191.2) * mm, "end": v(1190.9, 191.2) * mm});
            skFitSpline(sketch, "E818", {"points": [v(1952.52, 883.1) * mm, v(1629.12, 883.1) * mm, v(1564.78, 880.07) * mm, v(1506.74, 862.09) * mm]});
            skFitSpline(sketch, "E819", {"points": [v(1506.74, 862.09) * mm, v(1380.28, 822.9) * mm, v(1283.65, 728.12) * mm, v(1243.34, 603.74) * mm]});
            skFitSpline(sketch, "E820", {"points": [v(1243.34, 603.74) * mm, v(1227.99, 556.36) * mm, v(1221.98, 477.63) * mm, v(1217.9, 270.13) * mm]});
            skFitSpline(sketch, "E821", {"points": [v(1217.9, 270.13) * mm, v(1214.95, 120.75) * mm, v(1215.77, -9.85) * mm, v(1219.7, -20.1) * mm]});
            skFitSpline(sketch, "E822", {"points": [v(1219.7, -20.1) * mm, v(1225.03, -34) * mm, v(1241.6, -37.8) * mm, v(1284.89, -35.02) * mm]});
            skLineSegment(sketch, "E823", {"start": v(1349.02, 163.77) * mm, "end": v(1355.12, 358.85) * mm});
            skLineSegment(sketch, "E824", {"start": v(1355.12, 358.85) * mm, "end": v(1775.74, 358.85) * mm});
            skLineSegment(sketch, "E825", {"start": v(1775.74, 358.85) * mm, "end": v(2196.36, 358.85) * mm});
            skLineSegment(sketch, "E826", {"start": v(2196.36, 358.85) * mm, "end": v(2202.46, 163.77) * mm});
            skLineSegment(sketch, "E827", {"start": v(2202.46, 163.77) * mm, "end": v(2208.56, -31.3) * mm});
            skLineSegment(sketch, "E828", {"start": v(2208.56, -31.3) * mm, "end": v(2269.52, -31.3) * mm});
            skLineSegment(sketch, "E829", {"start": v(2269.52, -31.3) * mm, "end": v(2330.48, -31.3) * mm});
            skLineSegment(sketch, "E830", {"start": v(2330.48, -31.3) * mm, "end": v(2330.48, 425.9) * mm});
            skLineSegment(sketch, "E831", {"start": v(2330.48, 425.9) * mm, "end": v(2330.48, 883.1) * mm});
            skLineSegment(sketch, "E832", {"start": v(2330.48, 883.1) * mm, "end": v(1952.52, 883.1) * mm});
            skFitSpline(sketch, "E833", {"points": [v(1364.12, 540.82) * mm, v(1374.06, 629.03) * mm, v(1409.1, 683.86) * mm, v(1477.67, 718.5) * mm]});
            skFitSpline(sketch, "E834", {"points": [v(1477.67, 718.5) * mm, v(1536.94, 748.46) * mm, v(1543.8, 749.06) * mm, v(1870.65, 752.91) * mm]});
            skLineSegment(sketch, "E835", {"start": v(1284.89, -35.02) * mm, "end": v(1342.92, -31.3) * mm});
            skLineSegment(sketch, "E836", {"start": v(1342.92, -31.3) * mm, "end": v(1349.02, 163.77) * mm});
            skLineSegment(sketch, "E837", {"start": v(1870.65, 752.91) * mm, "end": v(2203.3, 756.84) * mm});
            skLineSegment(sketch, "E838", {"start": v(2203.3, 756.84) * mm, "end": v(2199.83, 624.9) * mm});
            skLineSegment(sketch, "E839", {"start": v(2199.83, 624.9) * mm, "end": v(2196.36, 492.96) * mm});
            skLineSegment(sketch, "E840", {"start": v(2196.36, 492.96) * mm, "end": v(1777.18, 489.75) * mm});
            skLineSegment(sketch, "E841", {"start": v(1777.18, 489.75) * mm, "end": v(1358, 486.54) * mm});
            skLineSegment(sketch, "E842", {"start": v(1358, 486.54) * mm, "end": v(1364.12, 540.82) * mm});
            skFitSpline(sketch, "E843", {"points": [v(1979.96, 734.98) * mm, v(1758, 744) * mm, v(1551.46, 728.93) * mm, v(1488.67, 699.14) * mm]});
            skFitSpline(sketch, "E844", {"points": [v(1488.67, 699.14) * mm, v(1440.48, 676.27) * mm, v(1399.49, 616.5) * mm, v(1389.41, 554.42) * mm]});
            skLineSegment(sketch, "E845", {"start": v(2178.08, 619.08) * mm, "end": v(2178.08, 726.92) * mm});
            skLineSegment(sketch, "E846", {"start": v(2178.08, 726.92) * mm, "end": v(1979.96, 734.98) * mm});
            skFitSpline(sketch, "E847", {"points": [v(-4195.57, 130.65) * mm, v(-4265.31, 194.2) * mm, v(-4289.06, 230.83) * mm, v(-4260.54, 230.83) * mm]});
            skFitSpline(sketch, "E848", {"points": [v(-4260.54, 230.83) * mm, v(-4242.82, 230.83) * mm, v(-4034.82, 154.69) * mm, v(-4022.25, 143.6) * mm]});
            skFitSpline(sketch, "E849", {"points": [v(-4022.25, 143.6) * mm, v(-4007.64, 130.72) * mm, v(-4073.89, 60) * mm, v(-4100.04, 60.55) * mm]});
            skFitSpline(sketch, "E850", {"points": [v(-4100.04, 60.55) * mm, v(-4110.52, 60.77) * mm, v(-4153.5, 92.32) * mm, v(-4195.57, 130.65) * mm]});
            skLineSegment(sketch, "E851", {"start": v(1389.41, 554.42) * mm, "end": v(1382.4, 511.25) * mm});
            skLineSegment(sketch, "E852", {"start": v(1382.4, 511.25) * mm, "end": v(1780.24, 511.25) * mm});
            skLineSegment(sketch, "E853", {"start": v(1780.24, 511.25) * mm, "end": v(2178.08, 511.25) * mm});
            skLineSegment(sketch, "E854", {"start": v(2178.08, 511.25) * mm, "end": v(2178.08, 619.08) * mm});
            skFitSpline(sketch, "E855", {"points": [v(-4071.4, 107.73) * mm, v(-4051.12, 130.13) * mm, v(-4052.83, 131.8) * mm, v(-4121.32, 156.56) * mm]});
            skFitSpline(sketch, "E856", {"points": [v(-4121.32, 156.56) * mm, v(-4160.33, 170.66) * mm, v(-4203.22, 187.87) * mm, v(-4216.63, 194.8) * mm]});
            skFitSpline(sketch, "E857", {"points": [v(-4216.63, 194.8) * mm, v(-4230.04, 201.74) * mm, v(-4210.84, 179.82) * mm, v(-4173.96, 146.1) * mm]});
            skFitSpline(sketch, "E858", {"points": [v(-4173.96, 146.1) * mm, v(-4137.08, 112.38) * mm, v(-4103.64, 84.73) * mm, v(-4099.65, 84.66) * mm]});
            skFitSpline(sketch, "E859", {"points": [v(-4099.65, 84.66) * mm, v(-4095.66, 84.58) * mm, v(-4082.94, 94.97) * mm, v(-4071.4, 107.73) * mm]});
            skFitSpline(sketch, "E860", {"points": [v(-4064.23, 407.61) * mm, v(-4141.34, 437.07) * mm, v(-4193.46, 461.86) * mm, v(-4180.05, 462.69) * mm]});
            skFitSpline(sketch, "E861", {"points": [v(-4180.05, 475.42) * mm, v(-4195.38, 482.48) * mm, v(-4136.55, 483.9) * mm, v(-4021.56, 479.24) * mm]});
            skFitSpline(sketch, "E862", {"points": [v(-4021.56, 479.24) * mm, v(-3920.97, 475.16) * mm, v(-3836.51, 469.84) * mm, v(-3833.87, 467.42) * mm]});
            skFitSpline(sketch, "E863", {"points": [v(-3833.87, 467.42) * mm, v(-3831.22, 465) * mm, v(-3838.54, 438.21) * mm, v(-3850.12, 407.89) * mm]});
            skFitSpline(sketch, "E864", {"points": [v(-3850.12, 407.89) * mm, v(-3876.62, 338.5) * mm, v(-3883.28, 338.49) * mm, v(-4064.23, 407.61) * mm]});
            skLineSegment(sketch, "E865", {"start": v(-4180.05, 462.69) * mm, "end": v(-4155.67, 464.2) * mm});
            skLineSegment(sketch, "E866", {"start": v(-4155.67, 464.2) * mm, "end": v(-4180.05, 475.42) * mm});
            skFitSpline(sketch, "E867", {"points": [v(-3879.1, 407.67) * mm, v(-3871.46, 424.46) * mm, v(-3868.75, 441.75) * mm, v(-3873.09, 446.1) * mm]});
            skFitSpline(sketch, "E868", {"points": [v(-3873.09, 446.1) * mm, v(-3877.43, 450.43) * mm, v(-3937.3, 456.05) * mm, v(-4006.13, 458.57) * mm]});
            skFitSpline(sketch, "E869", {"points": [v(-4027.65, 421.41) * mm, v(-3900.46, 370.19) * mm, v(-3896.36, 369.8) * mm, v(-3879.1, 407.67) * mm]});
            skLineSegment(sketch, "E870", {"start": v(-4006.13, 458.57) * mm, "end": v(-4131.28, 463.15) * mm});
            skLineSegment(sketch, "E871", {"start": v(-4131.28, 463.15) * mm, "end": v(-4027.65, 421.41) * mm});
            skFitSpline(sketch, "E872", {"points": [v(-6587.97, 617.82) * mm, v(-6587.97, 648.64) * mm, v(-6519.6, 834.36) * mm, v(-6474.59, 925.78) * mm]});
            skFitSpline(sketch, "E873", {"points": [v(-6474.59, 925.78) * mm, v(-6448.29, 979.2) * mm, v(-6427.63, 1006.13) * mm, v(-6411.19, 1008.4) * mm]});
            skFitSpline(sketch, "E874", {"points": [v(-6411.19, 1008.4) * mm, v(-6390.3, 1011.3) * mm, v(-5472.26, 679.77) * mm, v(-5455.92, 663.43) * mm]});
            skFitSpline(sketch, "E875", {"points": [v(-5455.92, 663.43) * mm, v(-5452.7, 660.2) * mm, v(-5457.83, 657.47) * mm, v(-5467.32, 657.37) * mm]});
            skFitSpline(sketch, "E876", {"points": [v(-5467.32, 657.37) * mm, v(-5481.55, 657.22) * mm, v(-5481.37, 655.1) * mm, v(-5466.3, 645.37) * mm]});
            skFitSpline(sketch, "E877", {"points": [v(-5466.3, 645.37) * mm, v(-5453.42, 637.04) * mm, v(-5470.5, 633.5) * mm, v(-5524.13, 633.36) * mm]});
            skFitSpline(sketch, "E878", {"points": [v(-5524.13, 633.36) * mm, v(-5621.9, 633.12) * mm, v(-6299.58, 611.27) * mm, v(-6463, 603.09) * mm]});
            skFitSpline(sketch, "E879", {"points": [v(-6463, 603.09) * mm, v(-6575.52, 597.45) * mm, v(-6587.97, 598.92) * mm, v(-6587.97, 617.82) * mm]});
            skLineSegment(sketch, "E880", {"start": v(-3879.1, 407.67) * mm, "end": v(-3879.1, 407.67) * mm});
            skFitSpline(sketch, "E881", {"points": [v(-5887.84, 645.83) * mm, v(-5687.17, 652.4) * mm, v(-5521.7, 659.1) * mm, v(-5520.12, 660.71) * mm]});
            skFitSpline(sketch, "E882", {"points": [v(-5520.12, 660.71) * mm, v(-5516.53, 664.39) * mm, v(-6395.68, 987.6) * mm, v(-6407.94, 987.1) * mm]});
            skFitSpline(sketch, "E883", {"points": [v(-6407.94, 987.1) * mm, v(-6421.6, 986.55) * mm, v(-6470.37, 883.96) * mm, v(-6519.41, 752.58) * mm]});
            skFitSpline(sketch, "E884", {"points": [v(-6519.41, 752.58) * mm, v(-6543.7, 687.5) * mm, v(-6563.59, 631.05) * mm, v(-6563.59, 627.16) * mm]});
            skFitSpline(sketch, "E885", {"points": [v(-6563.59, 627.16) * mm, v(-6563.59, 623.27) * mm, v(-6493.64, 623.19) * mm, v(-6408.14, 627) * mm]});
            skFitSpline(sketch, "E886", {"points": [v(-6408.14, 627) * mm, v(-6322.64, 630.78) * mm, v(-6088.5, 639.26) * mm, v(-5887.84, 645.83) * mm]});
            skFitSpline(sketch, "E887", {"points": [v(-4187.82, 702.32) * mm, v(-4175.84, 707.33) * mm, v(-4175.12, 711.7) * mm, v(-4185.22, 717.95) * mm]});
            skFitSpline(sketch, "E888", {"points": [v(-4185.22, 717.95) * mm, v(-4200.46, 727.36) * mm, v(-3852.7, 889.28) * mm, v(-3817.34, 889.24) * mm]});
            skFitSpline(sketch, "E889", {"points": [v(-3817.34, 889.24) * mm, v(-3799.08, 889.22) * mm, v(-3796, 877.05) * mm, v(-3796, 804.9) * mm]});
            skLineSegment(sketch, "E890", {"start": v(-5887.84, 645.83) * mm, "end": v(-5887.84, 645.83) * mm});
            skFitSpline(sketch, "E891", {"points": [v(-3884.4, 713.88) * mm, v(-4051.17, 701.2) * mm, v(-4204.43, 695.37) * mm, v(-4187.82, 702.32) * mm]});
            skLineSegment(sketch, "E892", {"start": v(-3796, 804.9) * mm, "end": v(-3796, 720.6) * mm});
            skLineSegment(sketch, "E893", {"start": v(-3796, 720.6) * mm, "end": v(-3884.4, 713.88) * mm});
            skFitSpline(sketch, "E894", {"points": [v(-3847.82, 737.8) * mm, v(-3823.8, 742.68) * mm, v(-3820.39, 750.9) * mm, v(-3820.39, 804.1) * mm]});
            skFitSpline(sketch, "E895", {"points": [v(-3820.39, 804.1) * mm, v(-3820.39, 837.5) * mm, v(-3821.91, 864.82) * mm, v(-3823.77, 864.82) * mm]});
            skFitSpline(sketch, "E896", {"points": [v(-3823.77, 864.82) * mm, v(-3825.63, 864.82) * mm, v(-3900.63, 832.24) * mm, v(-3990.43, 792.4) * mm]});
            skFitSpline(sketch, "E897", {"points": [v(-4014.48, 726.1) * mm, v(-3937.9, 729.47) * mm, v(-3862.9, 734.72) * mm, v(-3847.82, 737.8) * mm]});
            skLineSegment(sketch, "E898", {"start": v(-3990.43, 792.4) * mm, "end": v(-4153.7, 720) * mm});
            skLineSegment(sketch, "E899", {"start": v(-4153.7, 720) * mm, "end": v(-4014.48, 726.1) * mm});
            skFitSpline(sketch, "E900", {"points": [v(-5728.44, 1006.11) * mm, v(-5909.49, 1076.24) * mm, v(-6108.37, 1153.11) * mm, v(-6170.4, 1176.95) * mm]});
            skFitSpline(sketch, "E901", {"points": [v(-6170.4, 1176.95) * mm, v(-6232.42, 1200.78) * mm, v(-6283.17, 1227.24) * mm, v(-6283.17, 1235.74) * mm]});
            skFitSpline(sketch, "E902", {"points": [v(-6283.17, 1235.74) * mm, v(-6283.17, 1263.52) * mm, v(-6029.13, 1500.84) * mm, v(-6003.94, 1496.6) * mm]});
            skFitSpline(sketch, "E903", {"points": [v(-6003.94, 1496.6) * mm, v(-5972, 1491.2) * mm, v(-5371.1, 911.05) * mm, v(-5377.99, 892.25) * mm]});
            skFitSpline(sketch, "E904", {"points": [v(-5377.99, 892.25) * mm, v(-5381.06, 883.87) * mm, v(-5387.1, 877.37) * mm, v(-5391.41, 877.81) * mm]});
            skFitSpline(sketch, "E905", {"points": [v(-5391.41, 877.81) * mm, v(-5395.72, 878.25) * mm, v(-5547.39, 935.99) * mm, v(-5728.44, 1006.11) * mm]});
            skFitSpline(sketch, "E906", {"points": [v(-5586.47, 1075.41) * mm, v(-6010.64, 1488.04) * mm, v(-5998.75, 1477.45) * mm, v(-6022.87, 1464.15) * mm]});
            skFitSpline(sketch, "E907", {"points": [v(-6022.87, 1464.15) * mm, v(-6035.28, 1457.3) * mm, v(-6093.3, 1403.32) * mm, v(-6151.81, 1344.2) * mm]});
            skFitSpline(sketch, "E908", {"points": [v(-5840.91, 1076.05) * mm, v(-5611.41, 987.7) * mm, v(-5422.85, 915.01) * mm, v(-5421.88, 914.5) * mm]});
            skFitSpline(sketch, "E909", {"points": [v(-5421.88, 914.5) * mm, v(-5420.91, 914) * mm, v(-5494.98, 986.41) * mm, v(-5586.47, 1075.41) * mm]});
            skLineSegment(sketch, "E910", {"start": v(-6151.81, 1344.2) * mm, "end": v(-6258.2, 1236.68) * mm});
            skLineSegment(sketch, "E911", {"start": v(-6258.2, 1236.68) * mm, "end": v(-5840.91, 1076.05) * mm});
            skFitSpline(sketch, "E912", {"points": [v(-4305.91, 943.45) * mm, v(-4300.69, 966.86) * mm, v(-3989.31, 1303.73) * mm, v(-3972.9, 1303.73) * mm]});
            skFitSpline(sketch, "E913", {"points": [v(-3972.9, 1303.73) * mm, v(-3957.96, 1303.73) * mm, v(-3881.35, 1168.82) * mm, v(-3881.35, 1142.53) * mm]});
            skFitSpline(sketch, "E914", {"points": [v(-3881.35, 1142.53) * mm, v(-3881.35, 1131.37) * mm, v(-3959.67, 1087.14) * mm, v(-4089.1, 1025.2) * mm]});
            skFitSpline(sketch, "E915", {"points": [v(-4089.1, 1025.2) * mm, v(-4203.37, 970.52) * mm, v(-4299.79, 925.78) * mm, v(-4303.36, 925.78) * mm]});
            skFitSpline(sketch, "E916", {"points": [v(-4303.36, 925.78) * mm, v(-4306.93, 925.78) * mm, v(-4308.08, 933.73) * mm, v(-4305.91, 943.45) * mm]});
            skFitSpline(sketch, "E917", {"points": [v(-3936.29, 1206.35) * mm, v(-3953.24, 1239.8) * mm, v(-3970.42, 1267.16) * mm, v(-3974.48, 1267.16) * mm]});
            skFitSpline(sketch, "E918", {"points": [v(-3974.48, 1267.16) * mm, v(-3982.28, 1267.16) * mm, v(-4158.92, 1082.02) * mm, v(-4216.87, 1013.1) * mm]});
            skFitSpline(sketch, "E919", {"points": [v(-4216.87, 1013.1) * mm, v(-4249.9, 973.81) * mm, v(-4245.06, 975.42) * mm, v(-4078.28, 1058.96) * mm]});
            skFitSpline(sketch, "E920", {"points": [v(-5515.08, 1351.58) * mm, v(-5679.36, 1504.6) * mm, v(-5813.78, 1637.37) * mm, v(-5813.78, 1646.6) * mm]});
            skFitSpline(sketch, "E921", {"points": [v(-5813.78, 1646.6) * mm, v(-5813.78, 1664.74) * mm, v(-5574.85, 1791.41) * mm, v(-5540.64, 1791.41) * mm]});
            skFitSpline(sketch, "E922", {"points": [v(-5540.64, 1791.41) * mm, v(-5525.47, 1791.41) * mm, v(-5474.92, 1697.59) * mm, v(-5352.89, 1442.98) * mm]});
            skFitSpline(sketch, "E923", {"points": [v(-5352.89, 1442.98) * mm, v(-5261.04, 1251.34) * mm, v(-5185.9, 1089.5) * mm, v(-5185.9, 1083.32) * mm]});
            skFitSpline(sketch, "E924", {"points": [v(-5185.9, 1083.32) * mm, v(-5185.9, 1051.41) * mm, v(-5241.33, 1096.6) * mm, v(-5515.08, 1351.58) * mm]});
            skLineSegment(sketch, "E925", {"start": v(-4078.28, 1058.96) * mm, "end": v(-3905.47, 1145.53) * mm});
            skLineSegment(sketch, "E926", {"start": v(-3905.47, 1145.53) * mm, "end": v(-3936.29, 1206.35) * mm});
            skFitSpline(sketch, "E927", {"points": [v(-5267.71, 1209.25) * mm, v(-5291.52, 1257.86) * mm, v(-5362.02, 1403.25) * mm, v(-5424.38, 1532.33) * mm]});
            skFitSpline(sketch, "E928", {"points": [v(-5424.38, 1532.33) * mm, v(-5486.75, 1661.42) * mm, v(-5540.83, 1767.03) * mm, v(-5544.55, 1767.03) * mm]});
            skFitSpline(sketch, "E929", {"points": [v(-5544.55, 1767.03) * mm, v(-5565.47, 1767.03) * mm, v(-5782.84, 1649.82) * mm, v(-5779.65, 1640.26) * mm]});
            skFitSpline(sketch, "E930", {"points": [v(-5779.65, 1640.26) * mm, v(-5776.63, 1631.2) * mm, v(-5234.38, 1122.34) * mm, v(-5226.5, 1121.16) * mm]});
            skFitSpline(sketch, "E931", {"points": [v(-5226.5, 1121.16) * mm, v(-5225.36, 1121) * mm, v(-5243.9, 1160.63) * mm, v(-5267.71, 1209.25) * mm]});
            skFitSpline(sketch, "E932", {"points": [v(-4483.04, 1117.91) * mm, v(-4487.87, 1125.74) * mm, v(-4453.93, 1229.72) * mm, v(-4407.62, 1349) * mm]});
            skFitSpline(sketch, "E933", {"points": [v(-4407.62, 1349) * mm, v(-4361.3, 1468.27) * mm, v(-4316.12, 1586.44) * mm, v(-4307.2, 1611.58) * mm]});
            skFitSpline(sketch, "E934", {"points": [v(-4307.2, 1611.58) * mm, v(-4298.28, 1636.73) * mm, v(-4284.2, 1657.3) * mm, v(-4275.93, 1657.3) * mm]});
            skFitSpline(sketch, "E935", {"points": [v(-4275.93, 1657.3) * mm, v(-4256.93, 1657.3) * mm, v(-4101.02, 1521.32) * mm, v(-4101.2, 1504.9) * mm]});
            skFitSpline(sketch, "E936", {"points": [v(-4101.2, 1504.9) * mm, v(-4101.46, 1480.95) * mm, v(-4474.04, 1103.35) * mm, v(-4483.04, 1117.91) * mm]});
            skFitSpline(sketch, "E937", {"points": [v(-4189.75, 1559.22) * mm, v(-4223.64, 1589.7) * mm, v(-4256.97, 1614.63) * mm, v(-4263.8, 1614.63) * mm]});
            skFitSpline(sketch, "E938", {"points": [v(-4263.8, 1614.63) * mm, v(-4275, 1614.63) * mm, v(-4309.14, 1534.7) * mm, v(-4417.43, 1254.97) * mm]});
            skFitSpline(sketch, "E939", {"points": [v(-4996.3, 1223.47) * mm, v(-5005.25, 1244.15) * mm, v(-5073.75, 1392.3) * mm, v(-5148.51, 1552.7) * mm]});
            skFitSpline(sketch, "E940", {"points": [v(-5148.51, 1552.7) * mm, v(-5223.28, 1713.1) * mm, v(-5281.96, 1850.8) * mm, v(-5278.93, 1858.72) * mm]});
            skFitSpline(sketch, "E941", {"points": [v(-5278.93, 1858.72) * mm, v(-5272.5, 1875.48) * mm, v(-5177.54, 1888.7) * mm, v(-5062.36, 1888.84) * mm]});
            skLineSegment(sketch, "E942", {"start": v(-4417.43, 1254.97) * mm, "end": v(-4452.83, 1163.53) * mm});
            skLineSegment(sketch, "E943", {"start": v(-4452.83, 1163.53) * mm, "end": v(-4290.48, 1333.67) * mm});
            skLineSegment(sketch, "E944", {"start": v(-4290.48, 1333.67) * mm, "end": v(-4128.13, 1503.82) * mm});
            skLineSegment(sketch, "E945", {"start": v(-4128.13, 1503.82) * mm, "end": v(-4189.75, 1559.22) * mm});
            skFitSpline(sketch, "E946", {"points": [v(-4974.26, 1800.57) * mm, v(-4970.29, 1751.95) * mm, v(-4963.95, 1610.68) * mm, v(-4960.17, 1486.62) * mm]});
            skFitSpline(sketch, "E947", {"points": [v(-4960.17, 1486.62) * mm, v(-4956.4, 1362.57) * mm, v(-4950.7, 1244.15) * mm, v(-4947.5, 1223.48) * mm]});
            skFitSpline(sketch, "E948", {"points": [v(-4947.5, 1223.48) * mm, v(-4943.11, 1194.98) * mm, v(-4946.34, 1185.89) * mm, v(-4960.85, 1185.89) * mm]});
            skFitSpline(sketch, "E949", {"points": [v(-4960.85, 1185.89) * mm, v(-4971.38, 1185.89) * mm, v(-4987.33, 1202.8) * mm, v(-4996.3, 1223.48) * mm]});
            skLineSegment(sketch, "E950", {"start": v(-5062.36, 1888.84) * mm, "end": v(-4981.5, 1888.96) * mm});
            skLineSegment(sketch, "E951", {"start": v(-4981.5, 1888.96) * mm, "end": v(-4974.26, 1800.57) * mm});
            skFitSpline(sketch, "E952", {"points": [v(-4970.3, 1245.06) * mm, v(-4974.2, 1254.79) * mm, v(-4977.08, 1251.9) * mm, v(-4977.67, 1237.7) * mm]});
            skFitSpline(sketch, "E953", {"points": [v(-4977.67, 1237.7) * mm, v(-4978.2, 1224.84) * mm, v(-4975.31, 1217.64) * mm, v(-4971.26, 1221.7) * mm]});
            skFitSpline(sketch, "E954", {"points": [v(-4971.26, 1221.7) * mm, v(-4967.21, 1225.74) * mm, v(-4966.78, 1236.26) * mm, v(-4970.3, 1245.06) * mm]});
            skLineSegment(sketch, "E955", {"start": v(-4996.3, 1223.48) * mm, "end": v(-4996.3, 1223.47) * mm});
            skFitSpline(sketch, "E956", {"points": [v(-4984.07, 1544.53) * mm, v(-4988.7, 1697.08) * mm, v(-4995.22, 1831.5) * mm, v(-4998.57, 1843.23) * mm]});
            skFitSpline(sketch, "E957", {"points": [v(-4998.57, 1843.23) * mm, v(-5003.61, 1860.91) * mm, v(-5018.61, 1864.45) * mm, v(-5086.13, 1863.86) * mm]});
            skFitSpline(sketch, "E958", {"points": [v(-5086.13, 1863.86) * mm, v(-5130.94, 1863.48) * mm, v(-5187.84, 1859.36) * mm, v(-5212.56, 1854.72) * mm]});
            skFitSpline(sketch, "E959", {"points": [v(-5122.35, 1556.72) * mm, v(-5048, 1397.46) * mm, v(-4984.58, 1267.16) * mm, v(-4981.4, 1267.16) * mm]});
            skFitSpline(sketch, "E960", {"points": [v(-4981.4, 1267.16) * mm, v(-4978.24, 1267.16) * mm, v(-4979.43, 1391.97) * mm, v(-4984.07, 1544.53) * mm]});
            skLineSegment(sketch, "E961", {"start": v(-5212.56, 1854.72) * mm, "end": v(-5257.52, 1846.28) * mm});
            skLineSegment(sketch, "E962", {"start": v(-5257.52, 1846.28) * mm, "end": v(-5122.35, 1556.72) * mm});
            skFitSpline(sketch, "E963", {"points": [v(-4739.23, 1521.84) * mm, v(-4744.68, 1711.6) * mm, v(-4743.93, 1848.1) * mm, v(-4737.41, 1854.62) * mm]});
            skFitSpline(sketch, "E964", {"points": [v(-4737.41, 1854.62) * mm, v(-4724.32, 1867.72) * mm, v(-4509.24, 1790.56) * mm, v(-4509.24, 1772.77) * mm]});
            skFitSpline(sketch, "E965", {"points": [v(-4509.24, 1772.77) * mm, v(-4509.24, 1766.26) * mm, v(-4552.8, 1635.41) * mm, v(-4606.06, 1482) * mm]});
            skFitSpline(sketch, "E966", {"points": [v(-4606.06, 1482) * mm, v(-4672.14, 1291.62) * mm, v(-4705.5, 1210.32) * mm, v(-4711.1, 1225.96) * mm]});
            skFitSpline(sketch, "E967", {"points": [v(-4711.1, 1225.96) * mm, v(-4718.94, 1247.83) * mm, v(-4719.55, 1247.77) * mm, v(-4724.65, 1224.49) * mm]});
            skFitSpline(sketch, "E968", {"points": [v(-4724.65, 1224.49) * mm, v(-4727.58, 1211.08) * mm, v(-4734.14, 1344.88) * mm, v(-4739.22, 1521.84) * mm]});
            skFitSpline(sketch, "E969", {"points": [v(-4616.62, 1528.59) * mm, v(-4573.88, 1648.9) * mm, v(-4541.41, 1753.87) * mm, v(-4544.48, 1761.85) * mm]});
            skFitSpline(sketch, "E970", {"points": [v(-4544.48, 1761.85) * mm, v(-4549.3, 1774.43) * mm, v(-4685.58, 1828) * mm, v(-4712.77, 1828) * mm]});
            skFitSpline(sketch, "E971", {"points": [v(-4712.77, 1828) * mm, v(-4718.18, 1828) * mm, v(-4722.56, 1749.8) * mm, v(-4722.52, 1654.25) * mm]});
            skFitSpline(sketch, "E972", {"points": [v(-4722.52, 1654.25) * mm, v(-4722.45, 1465.95) * mm, v(-4709.97, 1262.18) * mm, v(-4700.33, 1291.57) * mm]});
            skFitSpline(sketch, "E973", {"points": [v(-4700.33, 1291.57) * mm, v(-4697.03, 1301.61) * mm, v(-4659.36, 1408.27) * mm, v(-4616.62, 1528.59) * mm]});
            skSolve(sketch);
        }
        {
            var Q0;
            Q0=makeQuery(id+"F0.imprint","IMPRINT",FACE,{"disambiguationData":[TD([[makeQuery(id+"F0.imprint","IMPRINT",EDGE,{"derivedFrom":sQuery(id+"F0.wireOp",EDGE,"E721")}),1.0]])]});
            extrude(context, id + "F1", {"entities" : qUnion([Q0]), "depth" : 127 * mm, "offsetDistance" : 25.4 * mm});
        }
        {
            var Q0;
            Q0=makeQuery(id+"F0.imprint","IMPRINT",FACE,{"disambiguationData":[TD([[makeQuery(id+"F0.imprint","IMPRINT",EDGE,{"derivedFrom":sQuery(id+"F0.wireOp",EDGE,"E699")}),-1.0]])]});
            extrude(context, id + "F2", {"entities" : qUnion([Q0]), "depth" : 127 * mm, "offsetDistance" : 25.4 * mm});
        }
        {
            var Q0;
            Q0=makeQuery(id+"F2.opExtrude","CAP_FACE",FACE,{"disambiguationData":[OSD([sQuery(id+"F0.wireOp",EDGE,"E699"),sQuery(id+"F0.wireOp",EDGE,"E700"),sQuery(id+"F0.wireOp",EDGE,"E701"),sQuery(id+"F0.wireOp",EDGE,"E702"),sQuery(id+"F0.wireOp",EDGE,"E703"),sQuery(id+"F0.wireOp",EDGE,"E704"),sQuery(id+"F0.wireOp",EDGE,"E705"),sQuery(id+"F0.wireOp",EDGE,"E706"),sQuery(id+"F0.wireOp",EDGE,"E707"),sQuery(id+"F0.wireOp",EDGE,"E708"),sQuery(id+"F0.wireOp",EDGE,"E709"),sQuery(id+"F0.wireOp",EDGE,"E710"),sQuery(id+"F0.wireOp",EDGE,"E711"),sQuery(id+"F0.wireOp",EDGE,"E712"),sQuery(id+"F0.wireOp",EDGE,"E713"),sQuery(id+"F0.wireOp",EDGE,"E714"),sQuery(id+"F0.wireOp",EDGE,"E715"),sQuery(id+"F0.wireOp",EDGE,"E716"),sQuery(id+"F0.wireOp",EDGE,"E717"),sQuery(id+"F0.wireOp",EDGE,"E718"),sQuery(id+"F0.wireOp",EDGE,"E719"),sQuery(id+"F0.wireOp",EDGE,"E720"),sQuery(id+"F0.wireOp",EDGE,"E721"),sQuery(id+"F0.wireOp",EDGE,"E722"),sQuery(id+"F0.wireOp",EDGE,"E723"),sQuery(id+"F0.wireOp",EDGE,"E724"),sQuery(id+"F0.wireOp",EDGE,"E725"),sQuery(id+"F0.wireOp",EDGE,"E726"),sQuery(id+"F0.wireOp",EDGE,"E727"),sQuery(id+"F0.wireOp",EDGE,"E728"),sQuery(id+"F0.wireOp",EDGE,"E729"),sQuery(id+"F0.wireOp",EDGE,"E730"),sQuery(id+"F0.wireOp",EDGE,"E731"),sQuery(id+"F0.wireOp",EDGE,"E732"),sQuery(id+"F0.wireOp",EDGE,"E733"),sQuery(id+"F0.wireOp",EDGE,"E734"),sQuery(id+"F0.wireOp",EDGE,"E735"),sQuery(id+"F0.wireOp",EDGE,"E736"),sQuery(id+"F0.wireOp",EDGE,"E737"),sQuery(id+"F0.wireOp",EDGE,"E738"),sQuery(id+"F0.wireOp",EDGE,"E739"),sQuery(id+"F0.wireOp",EDGE,"E740")])],"isStart":false});
            fillet(context, id + "F3", {"entities" : qUnion([Q0]), "radius" : 5.08 * mm, "tangentPropagation" : true, "allowEdgeOverflow" : false});
        }
    });
